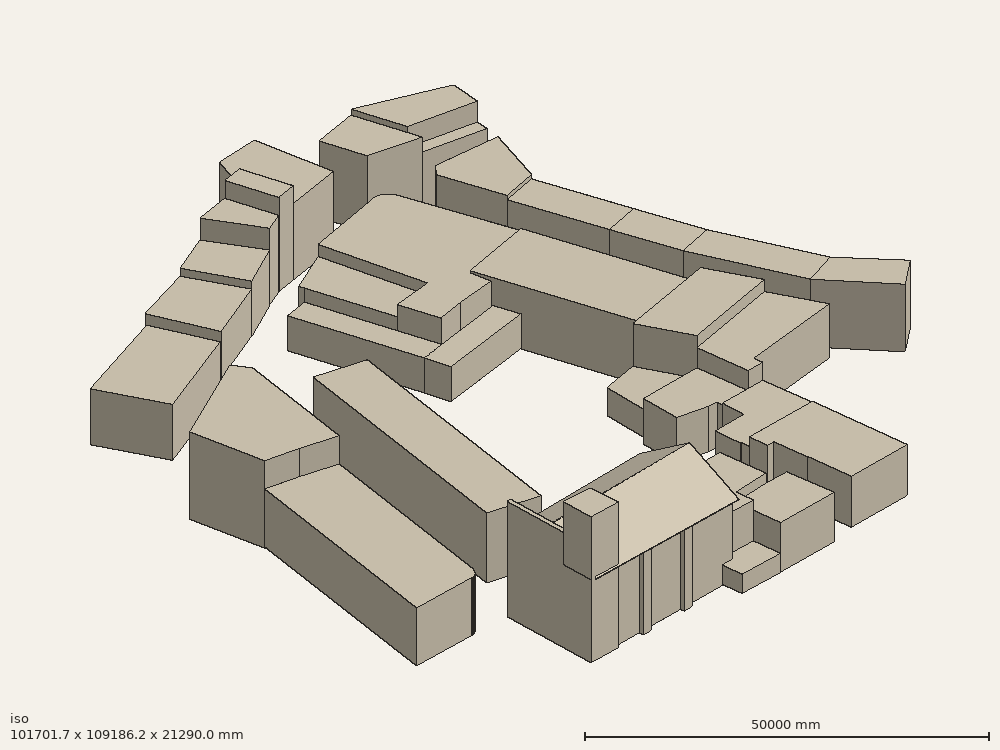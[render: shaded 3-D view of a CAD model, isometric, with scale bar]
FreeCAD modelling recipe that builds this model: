
FCSTD DOCUMENT  (FreeCAD 0.16R6563 (Git))
Label: Levantamento
License: All rights reserved
LicenseURL: http://en.wikipedia.org/wiki/All_rights_reserved
objects: App::Annotation×611, Part::Feature×158, Part::Part2DObjectPython×64, Part::Extrusion×37, App::DocumentObjectGroup×6, App::FeaturePython×4, Part::FeaturePython×3, Part::Cut×2, Part::Compound×1, Part::MultiFuse×1, App::DocumentObjectGroupPython×1
note: 269 computed .brp shape members not serialized (recipe doc carries the construction recipe); baked Part::Feature solids carry a one-line shape summary decoded from their .brp

FEATURE [App::Annotation] Text
  LabelText = TRAVESSA DE S.TIAGO
  Position = (-9.7511e+07,-6.33971e+07,25950)
FEATURE [App::Annotation] Text001
  LabelText = LARGO DR. JUSTINO FREIRE
  Position = (-9.75583e+07,-6.3388e+07,26154)
FEATURE [App::Annotation] Text002
  LabelText = RUA DO ALEIXO
  Position = (-9.75352e+07,-6.33613e+07,25958)
FEATURE [App::Annotation] Text003
  LabelText = RUA DO TERREIRINHO
  Position = (-9.75126e+07,-6.33096e+07,25667)
FEATURE [App::Annotation] Text004
  LabelText = RUA SERPA PINTO
  Position = (-9.74773e+07,-6.3325e+07,26806)
FEATURE [App::Annotation] Text005
  LabelText = IGREJA DE S. TIAGO
  Position = (-9.75165e+07,-6.33832e+07,25950)
FEATURE [App::Annotation] Text006
  LabelText = -97400
  Position = (-9.74009e+07,-6.34097e+07,0)
FEATURE [App::Annotation] Text007
  LabelText = -97450
  Position = (-9.74508e+07,-6.34097e+07,0)
FEATURE [App::Annotation] Text008
  LabelText = -97500
  Position = (-9.75009e+07,-6.34097e+07,0)
FEATURE [App::Annotation] Text009
  LabelText = -97550
  Position = (-9.75507e+07,-6.34097e+07,0)
FEATURE [App::Annotation] Text010
  LabelText = -63400
  Position = (-9.73992e+07,-6.33989e+07,0)
FEATURE [App::Annotation] Text011
  LabelText = -63350
  Position = (-9.73992e+07,-6.33486e+07,0)
FEATURE [App::Annotation] Text012
  LabelText = -63300
  Position = (-9.73992e+07,-6.32985e+07,0)
FEATURE [App::Annotation] Text013
  LabelText = VD
  Position = (-9.75235e+07,-6.33229e+07,0)
FEATURE [App::Annotation] Text014
  LabelText = 25.74
  Position = (-9.75242e+07,-6.33231e+07,0)
FEATURE [App::Annotation] Text015
  LabelText = IN
  Position = (-9.75237e+07,-6.33233e+07,0)
FEATURE [App::Annotation] Text016
  LabelText = 25.75
  Position = (-9.75244e+07,-6.33234e+07,0)
FEATURE [App::Annotation] Text017
  LabelText = LNMRVD
  Position = (-9.75268e+07,-6.3332e+07,0)
FEATURE [App::Annotation] Text018
  LabelText = 25.79
  Position = (-9.75274e+07,-6.33329e+07,0)
FEATURE [App::Annotation] Text019
  LabelText = LN
  Position = (-9.7528e+07,-6.33353e+07,0)
FEATURE [App::Annotation] Text020
  LabelText = 25.72
  Position = (-9.75287e+07,-6.33356e+07,0)
FEATURE [App::Annotation] Text021
  LabelText = 26.02
  Position = (-9.7542e+07,-6.33754e+07,0)
FEATURE [App::Annotation] Text022
  LabelText = CX
  Position = (-9.75309e+07,-6.33164e+07,0)
FEATURE [App::Annotation] Text023
  LabelText = 25.70
  Position = (-9.75313e+07,-6.33168e+07,0)
FEATURE [App::Annotation] Text024
  LabelText = CX
  Position = (-9.75307e+07,-6.33169e+07,0)
FEATURE [App::Annotation] Text025
  LabelText = 25.63
  Position = (-9.75311e+07,-6.33173e+07,0)
FEATURE [App::Annotation] Text026
  LabelText = CX
  Position = (-9.75311e+07,-6.3317e+07,0)
FEATURE [App::Annotation] Text027
  LabelText = 25.63
  Position = (-9.75315e+07,-6.33174e+07,0)
FEATURE [App::Annotation] Text028
  LabelText = CC
  Position = (-9.7534e+07,-6.33179e+07,0)
FEATURE [App::Annotation] Text029
  LabelText = 25.76
  Position = (-9.75346e+07,-6.33182e+07,0)
FEATURE [App::Annotation] Text030
  LabelText = OL
  Position = (-9.75349e+07,-6.33183e+07,0)
FEATURE [App::Annotation] Text031
  LabelText = 26.00
  Position = (-9.75356e+07,-6.33185e+07,0)
FEATURE [App::Annotation] Text032
  LabelText = OL
  Position = (-9.75364e+07,-6.3319e+07,0)
FEATURE [App::Annotation] Text033
  LabelText = 26.00
  Position = (-9.75371e+07,-6.33193e+07,0)
FEATURE [App::Annotation] Text034
  LabelText = LNCC
  Position = (-9.7539e+07,-6.33199e+07,0)
FEATURE [App::Annotation] Text035
  LabelText = 25.84
  Position = (-9.75396e+07,-6.33204e+07,0)
FEATURE [App::Annotation] Text036
  LabelText = LN
  Position = (-9.75385e+07,-6.33211e+07,0)
FEATURE [App::Annotation] Text037
  LabelText = 25.73
  Position = (-9.75392e+07,-6.33213e+07,0)
FEATURE [App::Annotation] Text038
  LabelText = CTT
  Position = (-9.75428e+07,-6.33239e+07,0)
FEATURE [App::Annotation] Text039
  LabelText = 25.88
  Position = (-9.75435e+07,-6.33242e+07,0)
FEATURE [App::Annotation] Text040
  LabelText = CTT
  Position = (-9.75436e+07,-6.33243e+07,0)
FEATURE [App::Annotation] Text041
  LabelText = 25.88
  Position = (-9.75442e+07,-6.33246e+07,0)
FEATURE [App::Annotation] Text042
  LabelText = CTT
  Position = (-9.75439e+07,-6.33237e+07,0)
FEATURE [App::Annotation] Text043
  LabelText = 25.87
  Position = (-9.75445e+07,-6.3324e+07,0)
FEATURE [App::Annotation] Text044
  LabelText = SOL
  Position = (-9.75449e+07,-6.33228e+07,0)
FEATURE [App::Annotation] Text045
  LabelText = 26.13
  Position = (-9.75455e+07,-6.33231e+07,0)
FEATURE [App::Annotation] Text046
  LabelText = LN
  Position = (-9.75498e+07,-6.33263e+07,0)
FEATURE [App::Annotation] Text047
  LabelText = 25.92
  Position = (-9.75505e+07,-6.33265e+07,0)
FEATURE [App::Annotation] Text048
  LabelText = CC
  Position = (-9.75503e+07,-6.33253e+07,0)
FEATURE [App::Annotation] Text049
  LabelText = 26.11
  Position = (-9.75509e+07,-6.33256e+07,0)
FEATURE [App::Annotation] Text050
  LabelText = OL
  Position = (-9.75518e+07,-6.3326e+07,0)
FEATURE [App::Annotation] Text051
  LabelText = 26.19
  Position = (-9.75524e+07,-6.33263e+07,0)
FEATURE [App::Annotation] Text052
  LabelText = CC
  Position = (-9.75559e+07,-6.33278e+07,0)
FEATURE [App::Annotation] Text053
  LabelText = 26.12
  Position = (-9.75565e+07,-6.3328e+07,0)
FEATURE [App::Annotation] Text054
  LabelText = LN
  Position = (-9.75554e+07,-6.33287e+07,0)
FEATURE [App::Annotation] Text055
  LabelText = 25.90
  Position = (-9.75561e+07,-6.33289e+07,0)
FEATURE [App::Annotation] Text056
  LabelText = INH
  Position = (-9.75539e+07,-6.3334e+07,0)
FEATURE [App::Annotation] Text057
  LabelText = 25.92
  Position = (-9.75546e+07,-6.33343e+07,0)
FEATURE [App::Annotation] Text058
  LabelText = INH
  Position = (-9.75549e+07,-6.33321e+07,0)
FEATURE [App::Annotation] Text059
  LabelText = 26.04
  Position = (-9.75555e+07,-6.33324e+07,0)
FEATURE [App::Annotation] Text060
  LabelText = INH
  Position = (-9.75501e+07,-6.33302e+07,0)
FEATURE [App::Annotation] Text061
  LabelText = 26.05
  Position = (-9.75508e+07,-6.33305e+07,0)
FEATURE [App::Annotation] Text062
  LabelText = INH
  Position = (-9.75369e+07,-6.33231e+07,0)
FEATURE [App::Annotation] Text063
  LabelText = 25.84
  Position = (-9.75376e+07,-6.33234e+07,0)
FEATURE [App::Annotation] Text064
  LabelText = INH
  Position = (-9.75357e+07,-6.33232e+07,0)
FEATURE [App::Annotation] Text065
  LabelText = 25.82
  Position = (-9.75363e+07,-6.33235e+07,0)
FEATURE [App::Annotation] Text066
  LabelText = INH
  Position = (-9.75336e+07,-6.33221e+07,0)
FEATURE [App::Annotation] Text067
  LabelText = 25.76
  Position = (-9.75343e+07,-6.33224e+07,0)
FEATURE [App::Annotation] Text068
  LabelText = OL
  Position = (-9.7533e+07,-6.33256e+07,0)
FEATURE [App::Annotation] Text069
  LabelText = 26.42
  Position = (-9.75337e+07,-6.33259e+07,0)
FEATURE [App::Annotation] Text070
  LabelText = IN
  Position = (-9.75314e+07,-6.33278e+07,0)
FEATURE [App::Annotation] Text071
  LabelText = 25.89
  Position = (-9.7532e+07,-6.33279e+07,0)
FEATURE [App::Annotation] Text072
  LabelText = CC
  Position = (-9.75315e+07,-6.33268e+07,0)
FEATURE [App::Annotation] Text073
  LabelText = 25.89
  Position = (-9.75322e+07,-6.33271e+07,0)
FEATURE [App::Annotation] Text074
  LabelText = CC
  Position = (-9.75329e+07,-6.33242e+07,0)
FEATURE [App::Annotation] Text075
  LabelText = 25.84
  Position = (-9.75336e+07,-6.33245e+07,0)
FEATURE [App::Annotation] Text076
  LabelText = CC
  Position = (-9.75382e+07,-6.33271e+07,0)
FEATURE [App::Annotation] Text077
  LabelText = 25.93
  Position = (-9.75388e+07,-6.33273e+07,0)
FEATURE [App::Annotation] Text078
  LabelText = UM
  Position = (-9.75385e+07,-6.33265e+07,0)
FEATURE [App::Annotation] Text079
  LabelText = 25.76
  Position = (-9.75392e+07,-6.33268e+07,0)
FEATURE [App::Annotation] Text080
  LabelText = UM
  Position = (-9.75319e+07,-6.33228e+07,0)
FEATURE [App::Annotation] Text081
  LabelText = 25.67
  Position = (-9.75326e+07,-6.33231e+07,0)
FEATURE [App::Annotation] Text082
  LabelText = UM
  Position = (-9.75313e+07,-6.33232e+07,0)
FEATURE [App::Annotation] Text083
  LabelText = 25.67
  Position = (-9.7532e+07,-6.33235e+07,0)
FEATURE [App::Annotation] Text084
  LabelText = LN
  Position = (-9.75323e+07,-6.33233e+07,0)
FEATURE [App::Annotation] Text085
  LabelText = 25.68
  Position = (-9.7533e+07,-6.33235e+07,0)
FEATURE [App::Annotation] Text086
  LabelText = LN
  Position = (-9.75315e+07,-6.33235e+07,0)
FEATURE [App::Annotation] Text087
  LabelText = 25.72
  Position = (-9.75322e+07,-6.33238e+07,0)
FEATURE [App::Annotation] Text088
  LabelText = LN
  Position = (-9.75305e+07,-6.33251e+07,0)
FEATURE [App::Annotation] Text089
  LabelText = 25.75
  Position = (-9.75311e+07,-6.33253e+07,0)
FEATURE [App::Annotation] Text090
  LabelText = LN
  Position = (-9.75301e+07,-6.33276e+07,0)
FEATURE [App::Annotation] Text091
  LabelText = 25.72
  Position = (-9.75307e+07,-6.33279e+07,0)
FEATURE [App::Annotation] Text092
  LabelText = VD
  Position = (-9.75244e+07,-6.33212e+07,0)
FEATURE [App::Annotation] Text093
  LabelText = 25.72
  Position = (-9.75251e+07,-6.33214e+07,0)
FEATURE [App::Annotation] Text094
  LabelText = CXD
  Position = (-9.75204e+07,-6.33159e+07,0)
FEATURE [App::Annotation] Text095
  LabelText = 25.67
  Position = (-9.75207e+07,-6.33163e+07,0)
FEATURE [App::Annotation] Text096
  LabelText = VD
  Position = (-9.75183e+07,-6.33166e+07,0)
FEATURE [App::Annotation] Text097
  LabelText = 25.58
  Position = (-9.7519e+07,-6.33169e+07,0)
FEATURE [App::Annotation] Text098
  LabelText = OL
  Position = (-9.75059e+07,-6.33029e+07,0)
FEATURE [App::Annotation] Text099
  LabelText = 25.84
  Position = (-9.75065e+07,-6.33031e+07,0)
FEATURE [App::Annotation] Text100
  LabelText = OL
  Position = (-9.75043e+07,-6.33022e+07,0)
FEATURE [App::Annotation] Text101
  LabelText = 25.94
  Position = (-9.75049e+07,-6.33025e+07,0)
FEATURE [App::Annotation] Text102
  LabelText = CXE
  Position = (-9.7504e+07,-6.33017e+07,0)
FEATURE [App::Annotation] Text103
  LabelText = 25.84
  Position = (-9.75043e+07,-6.33021e+07,0)
FEATURE [App::Annotation] Text104
  LabelText = CXE
  Position = (-9.75038e+07,-6.3302e+07,0)
FEATURE [App::Annotation] Text105
  LabelText = 25.79
  Position = (-9.75041e+07,-6.33024e+07,0)
FEATURE [App::Annotation] Text106
  LabelText = CXE
  Position = (-9.7503e+07,-6.33016e+07,0)
FEATURE [App::Annotation] Text107
  LabelText = 25.80
  Position = (-9.75033e+07,-6.3302e+07,0)
FEATURE [App::Annotation] Text108
  LabelText = OL
  Position = (-9.7499e+07,-6.32997e+07,0)
FEATURE [App::Annotation] Text109
  LabelText = 26.17
  Position = (-9.74996e+07,-6.32999e+07,0)
FEATURE [App::Annotation] Text110
  LabelText = CXD
  Position = (-9.75007e+07,-6.33004e+07,0)
FEATURE [App::Annotation] Text111
  LabelText = 25.85
  Position = (-9.7501e+07,-6.3301e+07,0)
FEATURE [App::Annotation] Text112
  LabelText = CXD
  Position = (-9.74978e+07,-6.32998e+07,0)
FEATURE [App::Annotation] Text113
  LabelText = 25.86
  Position = (-9.74982e+07,-6.33003e+07,0)
FEATURE [App::Annotation] Text114
  LabelText = UM
  Position = (-9.74967e+07,-6.33e+07,0)
FEATURE [App::Annotation] Text115
  LabelText = 25.80
  Position = (-9.74974e+07,-6.33003e+07,0)
FEATURE [App::Annotation] Text116
  LabelText = UM
  Position = (-9.74961e+07,-6.32999e+07,0)
FEATURE [App::Annotation] Text117
  LabelText = 25.79
  Position = (-9.74968e+07,-6.33001e+07,0)
FEATURE [App::Annotation] Text118
  LabelText = IN
  Position = (-9.74906e+07,-6.32984e+07,0)
FEATURE [App::Annotation] Text119
  LabelText = 26.00
  Position = (-9.74913e+07,-6.32985e+07,0)
FEATURE [App::Annotation] Text120
  LabelText = CC
  Position = (-9.74881e+07,-6.32975e+07,0)
FEATURE [App::Annotation] Text121
  LabelText = 26.01
  Position = (-9.74887e+07,-6.32978e+07,0)
FEATURE [App::Annotation] Text122
  LabelText = VD
  Position = (-9.74883e+07,-6.33016e+07,0)
FEATURE [App::Annotation] Text123
  LabelText = 26.02
  Position = (-9.7489e+07,-6.33019e+07,0)
FEATURE [App::Annotation] Text124
  LabelText = VD
  Position = (-9.74956e+07,-6.33036e+07,0)
FEATURE [App::Annotation] Text125
  LabelText = 25.93
  Position = (-9.74963e+07,-6.33039e+07,0)
FEATURE [App::Annotation] Text126
  LabelText = VD
  Position = (-9.74956e+07,-6.33036e+07,0)
FEATURE [App::Annotation] Text127
  LabelText = 25.93
  Position = (-9.74963e+07,-6.33039e+07,0)
FEATURE [App::Annotation] Text128
  LabelText = CXD
  Position = (-9.75007e+07,-6.33052e+07,0)
FEATURE [App::Annotation] Text129
  LabelText = 25.82
  Position = (-9.7501e+07,-6.33056e+07,0)
FEATURE [App::Annotation] Text130
  LabelText = VD
  Position = (-9.75015e+07,-6.33054e+07,0)
FEATURE [App::Annotation] Text131
  LabelText = 25.83
  Position = (-9.75022e+07,-6.33057e+07,0)
FEATURE [App::Annotation] Text132
  LabelText = VD
  Position = (-9.75047e+07,-6.33071e+07,0)
FEATURE [App::Annotation] Text133
  LabelText = 25.76
  Position = (-9.75053e+07,-6.33073e+07,0)
FEATURE [App::Annotation] Text134
  LabelText = CC
  Position = (-9.74996e+07,-6.33064e+07,0)
FEATURE [App::Annotation] Text135
  LabelText = 25.89
  Position = (-9.75003e+07,-6.33067e+07,0)
FEATURE [App::Annotation] Text136
  LabelText = VD
  Position = (-9.75005e+07,-6.33068e+07,0)
FEATURE [App::Annotation] Text137
  LabelText = 25.84
  Position = (-9.75012e+07,-6.3307e+07,0)
FEATURE [App::Annotation] Text138
  LabelText = MRVD
  Position = (-9.75264e+07,-6.33325e+07,0)
FEATURE [App::Annotation] Text139
  LabelText = 26.39
  Position = (-9.7527e+07,-6.33331e+07,0)
FEATURE [App::Annotation] Text140
  LabelText = CT
  Position = (-9.75249e+07,-6.33283e+07,0)
FEATURE [App::Annotation] Text141
  LabelText = 26.35
  Position = (-9.75255e+07,-6.33286e+07,0)
FEATURE [App::Annotation] Text142
  LabelText = CT
  Position = (-9.75222e+07,-6.33238e+07,0)
FEATURE [App::Annotation] Text143
  LabelText = 26.29
  Position = (-9.75229e+07,-6.3324e+07,0)
FEATURE [App::Annotation] Text144
  LabelText = CT
  Position = (-9.75189e+07,-6.33204e+07,0)
FEATURE [App::Annotation] Text145
  LabelText = 26.22
  Position = (-9.75196e+07,-6.33206e+07,0)
FEATURE [App::Annotation] Text146
  LabelText = CT
  Position = (-9.75162e+07,-6.33183e+07,0)
FEATURE [App::Annotation] Text147
  LabelText = 26.20
  Position = (-9.75169e+07,-6.33186e+07,0)
FEATURE [App::Annotation] Text148
  LabelText = CT
  Position = (-9.75164e+07,-6.33162e+07,0)
FEATURE [App::Annotation] Text149
  LabelText = 26.04
  Position = (-9.75171e+07,-6.33165e+07,0)
FEATURE [App::Annotation] Text150
  LabelText = CT
  Position = (-9.75151e+07,-6.33153e+07,0)
FEATURE [App::Annotation] Text151
  LabelText = 26.08
  Position = (-9.75157e+07,-6.33155e+07,0)
FEATURE [App::Annotation] Text152
  LabelText = IL
  Position = (-9.75163e+07,-6.33171e+07,0)
FEATURE [App::Annotation] Text153
  LabelText = 26.13
  Position = (-9.75169e+07,-6.33173e+07,0)
FEATURE [App::Annotation] Text154
  LabelText = IL
  Position = (-9.75157e+07,-6.3316e+07,0)
FEATURE [App::Annotation] Text155
  LabelText = 26.09
  Position = (-9.75164e+07,-6.33161e+07,0)
FEATURE [App::Annotation] Text156
  LabelText = CC
  Position = (-9.75107e+07,-6.33057e+07,0)
FEATURE [App::Annotation] Text157
  LabelText = 25.68
  Position = (-9.75113e+07,-6.3306e+07,0)
FEATURE [App::Annotation] Text158
  LabelText = AT
  Position = (-9.75124e+07,-6.33068e+07,0)
FEATURE [App::Annotation] Text159
  LabelText = 25.58
  Position = (-9.75131e+07,-6.33071e+07,0)
FEATURE [App::Annotation] Text160
  LabelText = OL
  Position = (-9.75161e+07,-6.33083e+07,0)
FEATURE [App::Annotation] Text161
  LabelText = 25.81
  Position = (-9.75167e+07,-6.33085e+07,0)
FEATURE [App::Annotation] Text162
  LabelText = AT
  Position = (-9.75195e+07,-6.33102e+07,0)
FEATURE [App::Annotation] Text163
  LabelText = 25.48
  Position = (-9.75202e+07,-6.33104e+07,0)
FEATURE [App::Annotation] Text164
  LabelText = CXCTT
  Position = (-9.75202e+07,-6.331e+07,0)
FEATURE [App::Annotation] Text165
  LabelText = 25.48
  Position = (-9.75202e+07,-6.33104e+07,0)
FEATURE [App::Annotation] Text166
  LabelText = CXCTT
  Position = (-9.75206e+07,-6.33102e+07,0)
FEATURE [App::Annotation] Text167
  LabelText = 25.47
  Position = (-9.75206e+07,-6.33106e+07,0)
FEATURE [App::Annotation] Text168
  LabelText = UM
  Position = (-9.75203e+07,-6.33103e+07,0)
FEATURE [App::Annotation] Text169
  LabelText = 25.38
  Position = (-9.7521e+07,-6.33106e+07,0)
FEATURE [App::Annotation] Text170
  LabelText = CC
  Position = (-9.75208e+07,-6.33104e+07,0)
FEATURE [App::Annotation] Text171
  LabelText = 25.47
  Position = (-9.75214e+07,-6.33106e+07,0)
FEATURE [App::Annotation] Text172
  LabelText = CTT
  Position = (-9.7521e+07,-6.33111e+07,0)
FEATURE [App::Annotation] Text173
  LabelText = 25.54
  Position = (-9.75216e+07,-6.33115e+07,0)
FEATURE [App::Annotation] Text174
  LabelText = CTT
  Position = (-9.75215e+07,-6.33114e+07,0)
FEATURE [App::Annotation] Text175
  LabelText = 25.57
  Position = (-9.75222e+07,-6.33118e+07,0)
FEATURE [App::Annotation] Text176
  LabelText = CTT
  Position = (-9.7522e+07,-6.33107e+07,0)
FEATURE [App::Annotation] Text177
  LabelText = 25.55
  Position = (-9.75226e+07,-6.3311e+07,0)
FEATURE [App::Annotation] Text178
  LabelText = CC
  Position = (-9.75249e+07,-6.33104e+07,0)
FEATURE [App::Annotation] Text179
  LabelText = 25.65
  Position = (-9.75256e+07,-6.33106e+07,0)
FEATURE [App::Annotation] Text180
  LabelText = OL
  Position = (-9.75244e+07,-6.33121e+07,0)
FEATURE [App::Annotation] Text181
  LabelText = 26.10
  Position = (-9.7525e+07,-6.33123e+07,0)
FEATURE [App::Annotation] Text182
  LabelText = G
  Position = (-9.7524e+07,-6.33116e+07,0)
FEATURE [App::Annotation] Text183
  LabelText = 25.61
  Position = (-9.75246e+07,-6.33117e+07,0)
FEATURE [App::Annotation] Text184
  LabelText = G
  Position = (-9.75238e+07,-6.33122e+07,0)
FEATURE [App::Annotation] Text185
  LabelText = G
  Position = (-9.7524e+07,-6.33123e+07,0)
FEATURE [App::Annotation] Text186
  LabelText = CC
  Position = (-9.75238e+07,-6.33134e+07,0)
FEATURE [App::Annotation] Text187
  LabelText = 25.54
  Position = (-9.75245e+07,-6.33136e+07,0)
FEATURE [App::Annotation] Text188
  LabelText = UM
  Position = (-9.75246e+07,-6.33138e+07,0)
FEATURE [App::Annotation] Text189
  LabelText = 25.52
  Position = (-9.75253e+07,-6.33141e+07,0)
FEATURE [App::Annotation] Text190
  LabelText = SOL
  Position = (-9.75262e+07,-6.33143e+07,0)
FEATURE [App::Annotation] Text191
  LabelText = 25.98
  Position = (-9.75268e+07,-6.33146e+07,0)
FEATURE [App::Annotation] Text192
  LabelText = CXE
  Position = (-9.75276e+07,-6.33148e+07,0)
FEATURE [App::Annotation] Text193
  LabelText = 25.69
  Position = (-9.75279e+07,-6.33152e+07,0)
FEATURE [App::Annotation] Text194
  LabelText = CXE
  Position = (-9.75275e+07,-6.33151e+07,0)
FEATURE [App::Annotation] Text195
  LabelText = 25.63
  Position = (-9.75278e+07,-6.33155e+07,0)
FEATURE [App::Annotation] Text196
  LabelText = CXE
  Position = (-9.75282e+07,-6.33154e+07,0)
FEATURE [App::Annotation] Text197
  LabelText = 25.63
  Position = (-9.75286e+07,-6.33158e+07,0)
FEATURE [App::Annotation] Text198
  LabelText = VD
  Position = (-9.75189e+07,-6.33146e+07,0)
FEATURE [App::Annotation] Text199
  LabelText = 25.64
  Position = (-9.75196e+07,-6.33149e+07,0)
FEATURE [App::Annotation] Text200
  LabelText = VD
  Position = (-9.75178e+07,-6.33139e+07,0)
FEATURE [App::Annotation] Text201
  LabelText = 25.69
  Position = (-9.75185e+07,-6.33141e+07,0)
FEATURE [App::Annotation] Text202
  LabelText = VD
  Position = (-9.75147e+07,-6.33122e+07,0)
FEATURE [App::Annotation] Text203
  LabelText = 25.65
  Position = (-9.75154e+07,-6.33124e+07,0)
FEATURE [App::Annotation] Text204
  LabelText = 25.59
  Position = (-9.75159e+07,-6.3314e+07,0)
FEATURE [App::Annotation] Text205
  LabelText = VD
  Position = (-9.75151e+07,-6.33139e+07,0)
FEATURE [App::Annotation] Text206
  LabelText = 25.60
  Position = (-9.75158e+07,-6.33142e+07,0)
FEATURE [App::Annotation] Text207
  LabelText = G
  Position = (-9.75151e+07,-6.33144e+07,0)
FEATURE [App::Annotation] Text208
  LabelText = 25.62
  Position = (-9.75158e+07,-6.33145e+07,0)
FEATURE [App::Annotation] Text209
  LabelText = G
  Position = (-9.7515e+07,-6.33146e+07,0)
FEATURE [App::Annotation] Text210
  LabelText = 25.81
  Position = (-9.75156e+07,-6.33147e+07,0)
FEATURE [App::Annotation] Text211
  LabelText = G
  Position = (-9.75148e+07,-6.3315e+07,0)
FEATURE [App::Annotation] Text212
  LabelText = 26.13
  Position = (-9.75154e+07,-6.33151e+07,0)
FEATURE [App::Annotation] Text213
  LabelText = G
  Position = (-9.75121e+07,-6.33136e+07,0)
FEATURE [App::Annotation] Text214
  LabelText = 26.12
  Position = (-9.75128e+07,-6.33137e+07,0)
FEATURE [App::Annotation] Text215
  LabelText = G
  Position = (-9.75123e+07,-6.33134e+07,0)
FEATURE [App::Annotation] Text216
  LabelText = 25.82
  Position = (-9.7513e+07,-6.33135e+07,0)
FEATURE [App::Annotation] Text217
  LabelText = G
  Position = (-9.75124e+07,-6.33131e+07,0)
FEATURE [App::Annotation] Text218
  LabelText = 25.65
  Position = (-9.75131e+07,-6.33132e+07,0)
FEATURE [App::Annotation] Text219
  LabelText = AMP
  Position = (-9.75137e+07,-6.33114e+07,0)
FEATURE [App::Annotation] Text220
  LabelText = 25.69
  Position = (-9.75144e+07,-6.33119e+07,0)
FEATURE [App::Annotation] Text221
  LabelText = AMP
  Position = (-9.75064e+07,-6.33077e+07,0)
FEATURE [App::Annotation] Text222
  LabelText = 25.77
  Position = (-9.75071e+07,-6.33081e+07,0)
FEATURE [App::Annotation] Text223
  LabelText = VD
  Position = (-9.7506e+07,-6.33096e+07,0)
FEATURE [App::Annotation] Text224
  LabelText = 25.99
  Position = (-9.75067e+07,-6.33099e+07,0)
FEATURE [App::Annotation] Text225
  LabelText = MR
  Position = (-9.7506e+07,-6.33102e+07,0)
FEATURE [App::Annotation] Text226
  LabelText = 26.07
  Position = (-9.75067e+07,-6.33104e+07,0)
FEATURE [App::Annotation] Text227
  LabelText = MRCC
  Position = (-9.75003e+07,-6.33069e+07,0)
FEATURE [App::Annotation] Text228
  LabelText = 26.23
  Position = (-9.7501e+07,-6.33075e+07,0)
FEATURE [App::Annotation] Text229
  LabelText = ESTMR
  Position = (-9.75051e+07,-6.33093e+07,0)
FEATURE [App::Annotation] Text230
  LabelText = 26.13
  Position = (-9.75051e+07,-6.33097e+07,0)
FEATURE [App::Annotation] Text231
  LabelText = EST
  Position = (-9.7502e+07,-6.33232e+07,0)
FEATURE [App::Annotation] Text232
  LabelText = 26.32
  Position = (-9.75023e+07,-6.33236e+07,0)
FEATURE [App::Annotation] Text233
  LabelText = CC
  Position = (-9.74969e+07,-6.33227e+07,0)
FEATURE [App::Annotation] Text234
  LabelText = 26.61
  Position = (-9.74975e+07,-6.3323e+07,0)
FEATURE [App::Annotation] Text235
  LabelText = IN20
  Position = (-9.74775e+07,-6.33355e+07,0)
FEATURE [App::Annotation] Text236
  LabelText = 26.83
  Position = (-9.74781e+07,-6.3336e+07,0)
FEATURE [App::Annotation] Text237
  LabelText = IN20
  Position = (-9.74755e+07,-6.33426e+07,0)
FEATURE [App::Annotation] Text238
  LabelText = 26.90
  Position = (-9.74762e+07,-6.3343e+07,0)
FEATURE [App::Annotation] Text239
  LabelText = IN20
  Position = (-9.74749e+07,-6.3345e+07,0)
FEATURE [App::Annotation] Text240
  LabelText = 26.90
  Position = (-9.74755e+07,-6.33455e+07,0)
FEATURE [App::Annotation] Text241
  LabelText = OL
  Position = (-9.7472e+07,-6.33367e+07,0)
FEATURE [App::Annotation] Text242
  LabelText = 26.86
  Position = (-9.74727e+07,-6.33369e+07,0)
FEATURE [App::Annotation] Text243
  LabelText = ESG
  Position = (-9.7474e+07,-6.33311e+07,0)
FEATURE [App::Annotation] Text244
  LabelText = 26.39
  Position = (-9.74743e+07,-6.33315e+07,0)
FEATURE [App::Annotation] Text245
  LabelText = OL
  Position = (-9.74741e+07,-6.3329e+07,0)
FEATURE [App::Annotation] Text246
  LabelText = 26.56
  Position = (-9.74748e+07,-6.33293e+07,0)
FEATURE [App::Annotation] Text247
  LabelText = OL
  Position = (-9.74748e+07,-6.33265e+07,0)
FEATURE [App::Annotation] Text248
  LabelText = 26.58
  Position = (-9.74754e+07,-6.33267e+07,0)
FEATURE [App::Annotation] Text249
  LabelText = OL
  Position = (-9.74762e+07,-6.33213e+07,0)
FEATURE [App::Annotation] Text250
  LabelText = 26.54
  Position = (-9.74768e+07,-6.33215e+07,0)
FEATURE [App::Annotation] Text251
  LabelText = CC
  Position = (-9.74793e+07,-6.33223e+07,0)
FEATURE [App::Annotation] Text252
  LabelText = 26.39
  Position = (-9.748e+07,-6.33225e+07,0)
FEATURE [App::Annotation] Text253
  LabelText = AT
  Position = (-9.74791e+07,-6.33222e+07,0)
FEATURE [App::Annotation] Text254
  LabelText = 26.35
  Position = (-9.74798e+07,-6.33225e+07,0)
FEATURE [App::Annotation] Text255
  LabelText = AT
  Position = (-9.74772e+07,-6.33305e+07,0)
FEATURE [App::Annotation] Text256
  LabelText = 26.52
  Position = (-9.74779e+07,-6.33307e+07,0)
FEATURE [App::Annotation] Text257
  LabelText = UM25
  Position = (-9.74767e+07,-6.33302e+07,0)
FEATURE [App::Annotation] Text258
  LabelText = 26.44
  Position = (-9.74774e+07,-6.33308e+07,0)
FEATURE [App::Annotation] Text259
  LabelText = UM25
  Position = (-9.74765e+07,-6.33309e+07,0)
FEATURE [App::Annotation] Text260
  LabelText = 26.47
  Position = (-9.74772e+07,-6.33315e+07,0)
FEATURE [App::Annotation] Text261
  LabelText = UM25
  Position = (-9.74765e+07,-6.33309e+07,0)
FEATURE [App::Annotation] Text262
  LabelText = 26.47
  Position = (-9.74772e+07,-6.33315e+07,0)
FEATURE [App::Annotation] Text263
  LabelText = CC
  Position = (-9.74772e+07,-6.33312e+07,0)
FEATURE [App::Annotation] Text264
  LabelText = 26.51
  Position = (-9.74778e+07,-6.33314e+07,0)
FEATURE [App::Annotation] Text265
  LabelText = AT
  Position = (-9.74769e+07,-6.33311e+07,0)
FEATURE [App::Annotation] Text266
  LabelText = 26.50
  Position = (-9.74776e+07,-6.33314e+07,0)
FEATURE [App::Annotation] Text267
  LabelText = AT
  Position = (-9.74755e+07,-6.33378e+07,0)
FEATURE [App::Annotation] Text268
  LabelText = 26.62
  Position = (-9.74761e+07,-6.33381e+07,0)
FEATURE [App::Annotation] Text269
  LabelText = AT
  Position = (-9.74751e+07,-6.33389e+07,0)
FEATURE [App::Annotation] Text270
  LabelText = 26.69
  Position = (-9.74758e+07,-6.33391e+07,0)
FEATURE [App::Annotation] Text271
  LabelText = CX
  Position = (-9.74751e+07,-6.33372e+07,0)
FEATURE [App::Annotation] Text272
  LabelText = 26.61
  Position = (-9.74754e+07,-6.33376e+07,0)
FEATURE [App::Annotation] Text273
  LabelText = OL
  Position = (-9.74711e+07,-6.33401e+07,0)
FEATURE [App::Annotation] Text274
  LabelText = 26.84
  Position = (-9.74718e+07,-6.33404e+07,0)
FEATURE [App::Annotation] Text275
  LabelText = UM25
  Position = (-9.74713e+07,-6.33411e+07,0)
FEATURE [App::Annotation] Text276
  LabelText = 26.71
  Position = (-9.74719e+07,-6.33416e+07,0)
FEATURE [App::Annotation] Text277
  LabelText = UM25
  Position = (-9.74711e+07,-6.33417e+07,0)
FEATURE [App::Annotation] Text278
  LabelText = 26.73
  Position = (-9.74718e+07,-6.33423e+07,0)
FEATURE [App::Annotation] Text279
  LabelText = CC
  Position = (-9.74707e+07,-6.3342e+07,0)
FEATURE [App::Annotation] Text280
  LabelText = 26.76
  Position = (-9.74714e+07,-6.33422e+07,0)
FEATURE [App::Annotation] Text281
  LabelText = OL
  Position = (-9.74678e+07,-6.33494e+07,0)
FEATURE [App::Annotation] Text282
  LabelText = 27.04
  Position = (-9.74685e+07,-6.33497e+07,0)
FEATURE [App::Annotation] Text283
  LabelText = CX
  Position = (-9.74687e+07,-6.33501e+07,0)
FEATURE [App::Annotation] Text284
  LabelText = 27.04
  Position = (-9.74691e+07,-6.33505e+07,0)
FEATURE [App::Annotation] Text285
  LabelText = CC
  Position = (-9.74661e+07,-6.33623e+07,0)
FEATURE [App::Annotation] Text286
  LabelText = 27.55
  Position = (-9.74668e+07,-6.33626e+07,0)
FEATURE [App::Annotation] Text287
  LabelText = OL
  Position = (-9.74678e+07,-6.33585e+07,0)
FEATURE [App::Annotation] Text288
  LabelText = 27.40
  Position = (-9.74685e+07,-6.33587e+07,0)
FEATURE [App::Annotation] Text289
  LabelText = OL
  Position = (-9.74727e+07,-6.33483e+07,0)
FEATURE [App::Annotation] Text290
  LabelText = 27.14
  Position = (-9.74734e+07,-6.33485e+07,0)
FEATURE [App::Annotation] Text291
  LabelText = CX
  Position = (-9.74726e+07,-6.33461e+07,0)
FEATURE [App::Annotation] Text292
  LabelText = 26.85
  Position = (-9.7473e+07,-6.33465e+07,0)
FEATURE [App::Annotation] Text293
  LabelText = UM25
  Position = (-9.74731e+07,-6.3345e+07,0)
FEATURE [App::Annotation] Text294
  LabelText = 26.81
  Position = (-9.74736e+07,-6.33456e+07,0)
FEATURE [App::Annotation] Text295
  LabelText = UM25
  Position = (-9.74729e+07,-6.33456e+07,0)
FEATURE [App::Annotation] Text296
  LabelText = 26.80
  Position = (-9.74736e+07,-6.33462e+07,0)
FEATURE [App::Annotation] Text297
  LabelText = AT
  Position = (-9.74731e+07,-6.33466e+07,0)
FEATURE [App::Annotation] Text298
  LabelText = 26.87
  Position = (-9.74737e+07,-6.33469e+07,0)
FEATURE [App::Annotation] Text299
  LabelText = CC
  Position = (-9.74731e+07,-6.3347e+07,0)
FEATURE [App::Annotation] Text300
  LabelText = 26.89
  Position = (-9.74738e+07,-6.33472e+07,0)
FEATURE [App::Annotation] Text301
  LabelText = CC
  Position = (-9.74733e+07,-6.33461e+07,0)
FEATURE [App::Annotation] Text302
  LabelText = 26.87
  Position = (-9.7474e+07,-6.33463e+07,0)
FEATURE [App::Annotation] Text303
  LabelText = CC30
  Position = (-9.74747e+07,-6.33462e+07,0)
FEATURE [App::Annotation] Text304
  LabelText = 26.91
  Position = (-9.74752e+07,-6.33467e+07,0)
FEATURE [App::Annotation] Text305
  LabelText = EST
  Position = (-9.75057e+07,-6.33385e+07,0)
FEATURE [App::Annotation] Text306
  LabelText = CC
  Position = (-9.75033e+07,-6.33238e+07,0)
FEATURE [App::Annotation] Text307
  LabelText = 26.29
  Position = (-9.75039e+07,-6.33241e+07,0)
FEATURE [App::Annotation] Text308
  LabelText = ESTA
  Position = (-9.75136e+07,-6.33216e+07,0)
FEATURE [App::Annotation] Text309
  LabelText = 26.22
  Position = (-9.75138e+07,-6.3322e+07,0)
FEATURE [App::Annotation] Text310
  LabelText = ESTA
  Position = (-9.75146e+07,-6.33204e+07,0)
FEATURE [App::Annotation] Text311
  LabelText = 26.22
  Position = (-9.75147e+07,-6.33208e+07,0)
FEATURE [App::Annotation] Text312
  LabelText = ESTA
  Position = (-9.75106e+07,-6.33181e+07,0)
FEATURE [App::Annotation] Text313
  LabelText = 26.19
  Position = (-9.75107e+07,-6.33185e+07,0)
FEATURE [App::Annotation] Text314
  LabelText = ESTA
  Position = (-9.75125e+07,-6.33137e+07,0)
FEATURE [App::Annotation] Text315
  LabelText = 26.09
  Position = (-9.75127e+07,-6.33141e+07,0)
FEATURE [App::Annotation] Text316
  LabelText = ESTA
  Position = (-9.75168e+07,-6.33177e+07,0)
FEATURE [App::Annotation] Text317
  LabelText = 26.15
  Position = (-9.75169e+07,-6.33181e+07,0)
FEATURE [App::Annotation] Text318
  LabelText = ESTA
  Position = (-9.75135e+07,-6.33216e+07,0)
FEATURE [App::Annotation] Text319
  LabelText = 26.22
  Position = (-9.75137e+07,-6.3322e+07,0)
FEATURE [App::Annotation] Text320
  LabelText = ESTA
  Position = (-9.75199e+07,-6.33285e+07,0)
FEATURE [App::Annotation] Text321
  LabelText = 26.34
  Position = (-9.75201e+07,-6.33289e+07,0)
FEATURE [App::Annotation] Text322
  LabelText = ESTA
  Position = (-9.75246e+07,-6.33266e+07,0)
FEATURE [App::Annotation] Text323
  LabelText = 26.29
  Position = (-9.75248e+07,-6.3327e+07,0)
FEATURE [App::Annotation] Text324
  LabelText = ESTA
  Position = (-9.75272e+07,-6.33333e+07,0)
FEATURE [App::Annotation] Text325
  LabelText = 26.37
  Position = (-9.75274e+07,-6.33337e+07,0)
FEATURE [App::Annotation] Text326
  LabelText = ESTA
  Position = (-9.75217e+07,-6.33327e+07,0)
FEATURE [App::Annotation] Text327
  LabelText = 26.38
  Position = (-9.75219e+07,-6.33331e+07,0)
FEATURE [App::Annotation] Text328
  LabelText = ESTA
  Position = (-9.75307e+07,-6.33502e+07,0)
FEATURE [App::Annotation] Text329
  LabelText = 26.37
  Position = (-9.75309e+07,-6.33506e+07,0)
FEATURE [App::Annotation] Text330
  LabelText = ESTA
  Position = (-9.75255e+07,-6.33497e+07,0)
FEATURE [App::Annotation] Text331
  LabelText = 26.34
  Position = (-9.75257e+07,-6.33501e+07,0)
FEATURE [App::Annotation] Text332
  LabelText = ESTA1
  Position = (-9.75292e+07,-6.33666e+07,0)
FEATURE [App::Annotation] Text333
  LabelText = 26.09
  Position = (-9.75293e+07,-6.3367e+07,0)
FEATURE [App::Annotation] Text334
  LabelText = ESTA1
  Position = (-9.75342e+07,-6.33669e+07,0)
FEATURE [App::Annotation] Text335
  LabelText = 26.08
  Position = (-9.75343e+07,-6.33673e+07,0)
FEATURE [App::Annotation] Text336
  LabelText = ESTA1
  Position = (-9.75059e+07,-6.33539e+07,0)
FEATURE [App::Annotation] Text337
  LabelText = 26.29
  Position = (-9.7506e+07,-6.33543e+07,0)
FEATURE [App::Annotation] Text338
  LabelText = ESTA1
  Position = (-9.75009e+07,-6.33537e+07,0)
FEATURE [App::Annotation] Text339
  LabelText = 26.37
  Position = (-9.7501e+07,-6.33541e+07,0)
FEATURE [App::Annotation] Text340
  LabelText = ESTA1
  Position = (-9.75013e+07,-6.33551e+07,0)
FEATURE [App::Annotation] Text341
  LabelText = 26.35
  Position = (-9.75014e+07,-6.33555e+07,0)
FEATURE [App::Annotation] Text342
  LabelText = ESTA1
  Position = (-9.7499e+07,-6.33554e+07,0)
FEATURE [App::Annotation] Text343
  LabelText = 26.41
  Position = (-9.74991e+07,-6.33558e+07,0)
FEATURE [App::Annotation] Text344
  LabelText = ESTA1
  Position = (-9.75019e+07,-6.33694e+07,0)
FEATURE [App::Annotation] Text345
  LabelText = 26.33
  Position = (-9.7502e+07,-6.33698e+07,0)
FEATURE [App::Annotation] Text346
  LabelText = ESTA1
  Position = (-9.75042e+07,-6.33689e+07,0)
FEATURE [App::Annotation] Text347
  LabelText = 26.31
  Position = (-9.75042e+07,-6.33693e+07,0)
FEATURE [App::Annotation] Text348
  LabelText = ESTA1
  Position = (-9.75046e+07,-6.33704e+07,0)
FEATURE [App::Annotation] Text349
  LabelText = 26.31
  Position = (-9.75046e+07,-6.33708e+07,0)
FEATURE [App::Annotation] Text350
  LabelText = ESTA1
  Position = (-9.75096e+07,-6.33706e+07,0)
FEATURE [App::Annotation] Text351
  LabelText = 26.24
  Position = (-9.75097e+07,-6.33715e+07,0)
FEATURE [App::Annotation] Text352
  LabelText = ESTA
  Position = (-9.7515e+07,-6.33713e+07,0)
FEATURE [App::Annotation] Text353
  LabelText = 26.19
  Position = (-9.75151e+07,-6.33722e+07,0)
FEATURE [App::Annotation] Text354
  LabelText = ESTA
  Position = (-9.75098e+07,-6.33473e+07,0)
FEATURE [App::Annotation] Text355
  LabelText = 26.37
  Position = (-9.751e+07,-6.33477e+07,0)
FEATURE [App::Annotation] Text356
  LabelText = ESTA
  Position = (-9.7514e+07,-6.33445e+07,0)
FEATURE [App::Annotation] Text357
  LabelText = 26.40
  Position = (-9.75142e+07,-6.33449e+07,0)
FEATURE [App::Annotation] Text358
  LabelText = ESTA
  Position = (-9.75182e+07,-6.33417e+07,0)
FEATURE [App::Annotation] Text359
  LabelText = 26.39
  Position = (-9.75184e+07,-6.33421e+07,0)
FEATURE [App::Annotation] Text360
  LabelText = ESTA
  Position = (-9.75156e+07,-6.33297e+07,0)
FEATURE [App::Annotation] Text361
  LabelText = 26.37
  Position = (-9.75158e+07,-6.33301e+07,0)
FEATURE [App::Annotation] Text362
  LabelText = ESTA
  Position = (-9.75134e+07,-6.33311e+07,0)
FEATURE [App::Annotation] Text363
  LabelText = 26.37
  Position = (-9.75136e+07,-6.33315e+07,0)
FEATURE [App::Annotation] Text364
  LabelText = ESTA
  Position = (-9.75125e+07,-6.33262e+07,0)
FEATURE [App::Annotation] Text365
  LabelText = 26.30
  Position = (-9.75127e+07,-6.33266e+07,0)
FEATURE [App::Annotation] Text366
  LabelText = ESTA
  Position = (-9.75061e+07,-6.33303e+07,0)
FEATURE [App::Annotation] Text367
  LabelText = 26.34
  Position = (-9.75063e+07,-6.33307e+07,0)
FEATURE [App::Annotation] Text368
  LabelText = EST
  Position = (-9.75055e+07,-6.3311e+07,0)
FEATURE [App::Annotation] Text369
  LabelText = 26.14
  Position = (-9.75065e+07,-6.33115e+07,0)
FEATURE [App::Annotation] Text370
  LabelText = ESTA
  Position = (-9.75e+07,-6.3334e+07,0)
FEATURE [App::Annotation] Text371
  LabelText = 26.46
  Position = (-9.75001e+07,-6.33344e+07,0)
FEATURE [App::Annotation] Text372
  LabelText = ESTA
  Position = (-9.75031e+07,-6.33302e+07,0)
FEATURE [App::Annotation] Text373
  LabelText = 26.35
  Position = (-9.75033e+07,-6.33306e+07,0)
FEATURE [App::Annotation] Text374
  LabelText = ESTA
  Position = (-9.74924e+07,-6.3328e+07,0)
FEATURE [App::Annotation] Text375
  LabelText = 26.65
  Position = (-9.74926e+07,-6.33284e+07,0)
FEATURE [App::Annotation] Text376
  LabelText = ESTA1
  Position = (-9.74896e+07,-6.33315e+07,0)
FEATURE [App::Annotation] Text377
  LabelText = 26.73
  Position = (-9.74897e+07,-6.33319e+07,0)
FEATURE [App::Annotation] Text378
  LabelText = ESTA
  Position = (-9.75049e+07,-6.33496e+07,0)
FEATURE [App::Annotation] Text379
  LabelText = 26.33
  Position = (-9.7505e+07,-6.335e+07,0)
FEATURE [App::Annotation] Text380
  LabelText = ESTA
  Position = (-9.75028e+07,-6.33394e+07,0)
FEATURE [App::Annotation] Text381
  LabelText = 26.38
  Position = (-9.7503e+07,-6.33398e+07,0)
FEATURE [App::Annotation] Text382
  LabelText = ESTA
  Position = (-9.74874e+07,-6.33358e+07,0)
FEATURE [App::Annotation] Text383
  LabelText = 26.82
  Position = (-9.74876e+07,-6.33362e+07,0)
FEATURE [App::Annotation] Text384
  LabelText = ESTA
  Position = (-9.74859e+07,-6.33402e+07,0)
FEATURE [App::Annotation] Text385
  LabelText = 26.85
  Position = (-9.74861e+07,-6.33406e+07,0)
FEATURE [App::Annotation] Text386
  LabelText = ESTA1
  Position = (-9.7487e+07,-6.33453e+07,0)
FEATURE [App::Annotation] Text387
  LabelText = 26.88
  Position = (-9.74871e+07,-6.33457e+07,0)
FEATURE [App::Annotation] Text388
  LabelText = ESTA
  Position = (-9.74752e+07,-6.33434e+07,0)
FEATURE [App::Annotation] Text389
  LabelText = 26.88
  Position = (-9.74753e+07,-6.33439e+07,0)
FEATURE [App::Annotation] Text390
  LabelText = ESTA
  Position = (-9.74803e+07,-6.33453e+07,0)
FEATURE [App::Annotation] Text391
  LabelText = 26.96
  Position = (-9.74805e+07,-6.33457e+07,0)
FEATURE [App::Annotation] Text392
  LabelText = ESTA
  Position = (-9.74849e+07,-6.33267e+07,0)
FEATURE [App::Annotation] Text393
  LabelText = 26.76
  Position = (-9.74851e+07,-6.33271e+07,0)
FEATURE [App::Annotation] Text394
  LabelText = ESTA
  Position = (-9.74808e+07,-6.33249e+07,0)
FEATURE [App::Annotation] Text395
  LabelText = 26.77
  Position = (-9.74809e+07,-6.33253e+07,0)
FEATURE [App::Annotation] Text396
  LabelText = LA
  Position = (-9.74935e+07,-6.33286e+07,0)
FEATURE [App::Annotation] Text397
  LabelText = 26.62
  Position = (-9.74942e+07,-6.33288e+07,0)
FEATURE [App::Annotation] Text398
  LabelText = LA
  Position = (-9.75015e+07,-6.33305e+07,0)
FEATURE [App::Annotation] Text399
  LabelText = CC
  Position = (-9.75017e+07,-6.33301e+07,0)
FEATURE [App::Annotation] Text400
  LabelText = 26.38
  Position = (-9.75024e+07,-6.33303e+07,0)
FEATURE [App::Annotation] Text401
  LabelText = CC
  Position = (-9.74973e+07,-6.3329e+07,0)
FEATURE [App::Annotation] Text402
  LabelText = 26.53
  Position = (-9.7498e+07,-6.33293e+07,0)
FEATURE [App::Annotation] Text403
  LabelText = CC
  Position = (-9.7491e+07,-6.3328e+07,0)
FEATURE [App::Annotation] Text404
  LabelText = 26.72
  Position = (-9.74917e+07,-6.33283e+07,0)
FEATURE [App::Annotation] Text405
  LabelText = VDCC
  Position = (-9.74806e+07,-6.33224e+07,0)
FEATURE [App::Annotation] Text406
  LabelText = 26.98
  Position = (-9.74813e+07,-6.3323e+07,0)
FEATURE [App::Annotation] Text407
  LabelText = VD
  Position = (-9.74788e+07,-6.33311e+07,0)
FEATURE [App::Annotation] Text408
  LabelText = 26.76
  Position = (-9.74794e+07,-6.33314e+07,0)
FEATURE [App::Annotation] Text409
  LabelText = VD
  Position = (-9.74778e+07,-6.33331e+07,0)
FEATURE [App::Annotation] Text410
  LabelText = 26.79
  Position = (-9.74785e+07,-6.33333e+07,0)
FEATURE [App::Annotation] Text411
  LabelText = VD
  Position = (-9.74762e+07,-6.33344e+07,0)
FEATURE [App::Annotation] Text412
  LabelText = 26.63
  Position = (-9.74769e+07,-6.33346e+07,0)
FEATURE [App::Annotation] Text413
  LabelText = CONTADOR
  Position = (-9.74801e+07,-6.33344e+07,0)
FEATURE [App::Annotation] Text414
  LabelText = 26.87
  Position = (-9.74807e+07,-6.33351e+07,0)
FEATURE [App::Annotation] Text415
  LabelText = EST
  Position = (-9.74739e+07,-6.33358e+07,0)
FEATURE [App::Annotation] Text416
  LabelText = 26.61
  Position = (-9.74742e+07,-6.33352e+07,0)
FEATURE [App::Annotation] Text417
  LabelText = CC1
  Position = (-9.74875e+07,-6.33497e+07,0)
FEATURE [App::Annotation] Text418
  LabelText = 26.84
  Position = (-9.74881e+07,-6.33501e+07,0)
FEATURE [App::Annotation] Text419
  LabelText = CC1
  Position = (-9.74951e+07,-6.33518e+07,0)
FEATURE [App::Annotation] Text420
  LabelText = 26.69
  Position = (-9.74955e+07,-6.3352e+07,0)
FEATURE [App::Annotation] Text421
  LabelText = CC1
  Position = (-9.74949e+07,-6.33803e+07,0)
FEATURE [App::Annotation] Text422
  LabelText = 26.53
  Position = (-9.74956e+07,-6.33807e+07,0)
FEATURE [App::Annotation] Text423
  LabelText = CC1
  Position = (-9.74931e+07,-6.33927e+07,0)
FEATURE [App::Annotation] Text424
  LabelText = 26.60
  Position = (-9.74936e+07,-6.3393e+07,0)
FEATURE [App::Annotation] Text425
  LabelText = CC
  Position = (-9.74967e+07,-6.33856e+07,0)
FEATURE [App::Annotation] Text426
  LabelText = 26.56
  Position = (-9.74974e+07,-6.33859e+07,0)
FEATURE [App::Annotation] Text427
  LabelText = EST
  Position = (-9.74989e+07,-6.33722e+07,0)
FEATURE [App::Annotation] Text428
  LabelText = 26.41
  Position = (-9.74991e+07,-6.33715e+07,0)
FEATURE [App::Annotation] Text429
  LabelText = EST
  Position = (-9.7506e+07,-6.33433e+07,0)
FEATURE [App::Annotation] Text430
  LabelText = 26.38
  Position = (-9.75062e+07,-6.33426e+07,0)
FEATURE [App::Annotation] Text431
  LabelText = 26.37
  Position = (-9.75059e+07,-6.33377e+07,0)
FEATURE [App::Annotation] Text432
  LabelText = CC17
  Position = (-9.74952e+07,-6.33756e+07,0)
FEATURE [App::Annotation] Text433
  LabelText = 26.48
  Position = (-9.74958e+07,-6.33761e+07,0)
FEATURE [App::Annotation] Text434
  LabelText = CC
  Position = (-9.75012e+07,-6.33733e+07,0)
FEATURE [App::Annotation] Text435
  LabelText = 26.34
  Position = (-9.75018e+07,-6.33736e+07,0)
FEATURE [App::Annotation] Text436
  LabelText = OL
  Position = (-9.75341e+07,-6.33344e+07,0)
FEATURE [App::Annotation] Text437
  LabelText = 26.31
  Position = (-9.75347e+07,-6.33347e+07,0)
FEATURE [App::Annotation] Text438
  LabelText = OL
  Position = (-9.75352e+07,-6.33395e+07,0)
FEATURE [App::Annotation] Text439
  LabelText = 26.40
  Position = (-9.75359e+07,-6.33397e+07,0)
FEATURE [App::Annotation] Text440
  LabelText = OL
  Position = (-9.75368e+07,-6.335e+07,0)
FEATURE [App::Annotation] Text441
  LabelText = 26.32
  Position = (-9.75375e+07,-6.33503e+07,0)
FEATURE [App::Annotation] Text442
  LabelText = OL
  Position = (-9.75384e+07,-6.33561e+07,0)
FEATURE [App::Annotation] Text443
  LabelText = 26.33
  Position = (-9.75391e+07,-6.33563e+07,0)
FEATURE [App::Annotation] Text444
  LabelText = OL
  Position = (-9.75397e+07,-6.33628e+07,0)
FEATURE [App::Annotation] Text445
  LabelText = 26.32
  Position = (-9.75404e+07,-6.3363e+07,0)
FEATURE [App::Annotation] Text446
  LabelText = OL
  Position = (-9.75413e+07,-6.33692e+07,0)
FEATURE [App::Annotation] Text447
  LabelText = 26.32
  Position = (-9.7542e+07,-6.33695e+07,0)
FEATURE [App::Annotation] Text448
  LabelText = OL
  Position = (-9.75436e+07,-6.3377e+07,0)
FEATURE [App::Annotation] Text449
  LabelText = 26.31
  Position = (-9.75442e+07,-6.33773e+07,0)
FEATURE [App::Annotation] Text450
  LabelText = EST
  Position = (-9.75417e+07,-6.3375e+07,0)
FEATURE [App::Annotation] Text451
  LabelText = LN
  Position = (-9.75355e+07,-6.33694e+07,0)
FEATURE [App::Annotation] Text452
  LabelText = 25.80
  Position = (-9.75362e+07,-6.33697e+07,0)
FEATURE [App::Annotation] Text453
  LabelText = EL
  Position = (-9.75339e+07,-6.33679e+07,0)
FEATURE [App::Annotation] Text454
  LabelText = 26.12
  Position = (-9.75346e+07,-6.33681e+07,0)
FEATURE [App::Annotation] Text455
  LabelText = IN
  Position = (-9.75341e+07,-6.33686e+07,0)
FEATURE [App::Annotation] Text456
  LabelText = 26.10
  Position = (-9.75347e+07,-6.33687e+07,0)
FEATURE [App::Annotation] Text457
  LabelText = MR30
  Position = (-9.75347e+07,-6.33683e+07,0)
FEATURE [App::Annotation] Text458
  LabelText = 25.89
  Position = (-9.75354e+07,-6.33689e+07,0)
FEATURE [App::Annotation] Text459
  LabelText = CC
  Position = (-9.75423e+07,-6.33759e+07,0)
FEATURE [App::Annotation] Text460
  LabelText = 26.01
  Position = (-9.75429e+07,-6.33761e+07,0)
FEATURE [App::Annotation] Text461
  LabelText = CC
  Position = (-9.75428e+07,-6.33768e+07,0)
FEATURE [App::Annotation] Text462
  LabelText = 25.98
  Position = (-9.75434e+07,-6.3377e+07,0)
FEATURE [App::Annotation] Text463
  LabelText = LN
  Position = (-9.75434e+07,-6.33787e+07,0)
FEATURE [App::Annotation] Text464
  LabelText = 25.75
  Position = (-9.75441e+07,-6.33789e+07,0)
FEATURE [App::Annotation] Text465
  LabelText = LN
  Position = (-9.75421e+07,-6.33784e+07,0)
FEATURE [App::Annotation] Text466
  LabelText = 25.75
  Position = (-9.75427e+07,-6.33786e+07,0)
FEATURE [App::Annotation] Text467
  LabelText = LN
  Position = (-9.75411e+07,-6.33776e+07,0)
FEATURE [App::Annotation] Text468
  LabelText = 25.75
  Position = (-9.75418e+07,-6.33778e+07,0)
FEATURE [App::Annotation] Text469
  LabelText = EST
  Position = (-9.75287e+07,-6.33165e+07,0)
FEATURE [App::Annotation] Text470
  LabelText = 25.63
  Position = (-9.75289e+07,-6.33172e+07,0)
FEATURE [App::Annotation] Text471
  LabelText = CXA
  Position = (-9.75259e+07,-6.33149e+07,0)
FEATURE [App::Annotation] Text472
  LabelText = 25.58
  Position = (-9.75262e+07,-6.33153e+07,0)
FEATURE [App::Annotation] Text473
  LabelText = CXA
  Position = (-9.75249e+07,-6.33171e+07,0)
FEATURE [App::Annotation] Text474
  LabelText = 25.67
  Position = (-9.75252e+07,-6.33175e+07,0)
FEATURE [App::Annotation] Text475
  LabelText = CXD
  Position = (-9.75267e+07,-6.33196e+07,0)
FEATURE [App::Annotation] Text476
  LabelText = 25.69
  Position = (-9.7527e+07,-6.33201e+07,0)
FEATURE [App::Annotation] Text477
  LabelText = VD
  Position = (-9.75251e+07,-6.33223e+07,0)
FEATURE [App::Annotation] Text478
  LabelText = 25.68
  Position = (-9.75258e+07,-6.33226e+07,0)
FEATURE [App::Annotation] Text479
  LabelText = CXD
  Position = (-9.75291e+07,-6.33237e+07,0)
FEATURE [App::Annotation] Text480
  LabelText = 25.71
  Position = (-9.75294e+07,-6.33241e+07,0)
FEATURE [App::Annotation] Text481
  LabelText = UM25
  Position = (-9.75314e+07,-6.33351e+07,0)
FEATURE [App::Annotation] Text482
  LabelText = 25.63
  Position = (-9.75321e+07,-6.33357e+07,0)
FEATURE [App::Annotation] Text483
  LabelText = UM25
  Position = (-9.75313e+07,-6.33344e+07,0)
FEATURE [App::Annotation] Text484
  LabelText = 25.62
  Position = (-9.75319e+07,-6.3335e+07,0)
FEATURE [App::Annotation] Text485
  LabelText = UM25
  Position = (-9.75284e+07,-6.33347e+07,0)
FEATURE [App::Annotation] Text486
  LabelText = 25.63
  Position = (-9.7529e+07,-6.33352e+07,0)
FEATURE [App::Annotation] Text487
  LabelText = UM25
  Position = (-9.75286e+07,-6.33353e+07,0)
FEATURE [App::Annotation] Text488
  LabelText = 25.63
  Position = (-9.75292e+07,-6.33358e+07,0)
FEATURE [App::Annotation] Text489
  LabelText = CXD
  Position = (-9.7531e+07,-6.33399e+07,0)
FEATURE [App::Annotation] Text490
  LabelText = 25.73
  Position = (-9.75313e+07,-6.33403e+07,0)
FEATURE [App::Annotation] Text491
  LabelText = CXA
  Position = (-9.75337e+07,-6.33483e+07,0)
FEATURE [App::Annotation] Text492
  LabelText = 25.74
  Position = (-9.7534e+07,-6.33488e+07,0)
FEATURE [App::Annotation] Text493
  LabelText = UM25
  Position = (-9.75346e+07,-6.33492e+07,0)
FEATURE [App::Annotation] Text494
  LabelText = 25.64
  Position = (-9.75352e+07,-6.33498e+07,0)
FEATURE [App::Annotation] Text495
  LabelText = UM25
  Position = (-9.75347e+07,-6.33498e+07,0)
FEATURE [App::Annotation] Text496
  LabelText = 25.65
  Position = (-9.75354e+07,-6.33504e+07,0)
FEATURE [App::Annotation] Text497
  LabelText = UM25
  Position = (-9.75319e+07,-6.33506e+07,0)
FEATURE [App::Annotation] Text498
  LabelText = 25.66
  Position = (-9.75325e+07,-6.33512e+07,0)
FEATURE [App::Annotation] Text499
  LabelText = UM25
  Position = (-9.75317e+07,-6.335e+07,0)
FEATURE [App::Annotation] Text500
  LabelText = 25.67
  Position = (-9.75324e+07,-6.33505e+07,0)
FEATURE [App::Annotation] Text501
  LabelText = VD
  Position = (-9.75314e+07,-6.33498e+07,0)
FEATURE [App::Annotation] Text502
  LabelText = 25.64
  Position = (-9.75321e+07,-6.335e+07,0)
FEATURE [App::Annotation] Text503
  LabelText = VD
  Position = (-9.75349e+07,-6.33655e+07,0)
FEATURE [App::Annotation] Text504
  LabelText = 25.75
  Position = (-9.75364e+07,-6.33657e+07,0)
FEATURE [App::Annotation] Text505
  LabelText = UM25
  Position = (-9.75352e+07,-6.33658e+07,0)
FEATURE [App::Annotation] Text506
  LabelText = 25.74
  Position = (-9.75358e+07,-6.33663e+07,0)
FEATURE [App::Annotation] Text507
  LabelText = UM25
  Position = (-9.75353e+07,-6.33664e+07,0)
FEATURE [App::Annotation] Text508
  LabelText = 25.74
  Position = (-9.7536e+07,-6.3367e+07,0)
FEATURE [App::Annotation] Text509
  LabelText = UM25
  Position = (-9.75381e+07,-6.33651e+07,0)
FEATURE [App::Annotation] Text510
  LabelText = 25.70
  Position = (-9.75387e+07,-6.33657e+07,0)
FEATURE [App::Annotation] Text511
  LabelText = UM25
  Position = (-9.75382e+07,-6.33658e+07,0)
FEATURE [App::Annotation] Text512
  LabelText = 25.70
  Position = (-9.75388e+07,-6.33663e+07,0)
FEATURE [App::Annotation] Text513
  LabelText = CXA
  Position = (-9.75394e+07,-6.3373e+07,0)
FEATURE [App::Annotation] Text514
  LabelText = 25.79
  Position = (-9.75397e+07,-6.33734e+07,0)
FEATURE [App::Annotation] Text515
  LabelText = UM25
  Position = (-9.75412e+07,-6.33778e+07,0)
FEATURE [App::Annotation] Text516
  LabelText = 25.71
  Position = (-9.75417e+07,-6.33784e+07,0)
FEATURE [App::Annotation] Text517
  LabelText = UM25
  Position = (-9.75417e+07,-6.33783e+07,0)
FEATURE [App::Annotation] Text518
  LabelText = 25.72
  Position = (-9.75423e+07,-6.33789e+07,0)
FEATURE [App::Annotation] Text519
  LabelText = CX
  Position = (-9.75411e+07,-6.33968e+07,0)
FEATURE [App::Annotation] Text520
  LabelText = 25.97
  Position = (-9.75415e+07,-6.33972e+07,0)
FEATURE [App::Annotation] Text521
  LabelText = CC
  Position = (-9.75383e+07,-6.33929e+07,0)
FEATURE [App::Annotation] Text522
  LabelText = 25.86
  Position = (-9.7539e+07,-6.33932e+07,0)
FEATURE [App::Annotation] Text523
  LabelText = CX
  Position = (-9.75414e+07,-6.3386e+07,0)
FEATURE [App::Annotation] Text524
  LabelText = 25.84
  Position = (-9.75419e+07,-6.33864e+07,0)
FEATURE [App::Annotation] Text525
  LabelText = OL
  Position = (-9.75374e+07,-6.33856e+07,0)
FEATURE [App::Annotation] Text526
  LabelText = 25.94
  Position = (-9.75381e+07,-6.33858e+07,0)
FEATURE [App::Annotation] Text527
  LabelText = CC
  Position = (-9.75459e+07,-6.33963e+07,0)
FEATURE [App::Annotation] Text528
  LabelText = 25.95
  Position = (-9.75466e+07,-6.33966e+07,0)
FEATURE [App::Annotation] Text529
  LabelText = LN
  Position = (-9.75463e+07,-6.33948e+07,0)
FEATURE [App::Annotation] Text530
  LabelText = 25.83
  Position = (-9.7547e+07,-6.3395e+07,0)
FEATURE [App::Annotation] Text531
  LabelText = LNS
  Position = (-9.75404e+07,-6.33928e+07,0)
FEATURE [App::Annotation] Text532
  LabelText = 25.87
  Position = (-9.75411e+07,-6.33932e+07,0)
FEATURE [App::Annotation] Text533
  LabelText = UM25
  Position = (-9.75392e+07,-6.33803e+07,0)
FEATURE [App::Annotation] Text534
  LabelText = 25.67
  Position = (-9.75398e+07,-6.33808e+07,0)
FEATURE [App::Annotation] Text535
  LabelText = UM25
  Position = (-9.75391e+07,-6.33796e+07,0)
FEATURE [App::Annotation] Text536
  LabelText = 25.67
  Position = (-9.75398e+07,-6.33801e+07,0)
FEATURE [App::Annotation] Text537
  LabelText = LN
  Position = (-9.75386e+07,-6.33793e+07,0)
FEATURE [App::Annotation] Text538
  LabelText = 25.76
  Position = (-9.75393e+07,-6.33795e+07,0)
FEATURE [App::Annotation] Text539
  LabelText = LN
  Position = (-9.75382e+07,-6.33783e+07,0)
FEATURE [App::Annotation] Text540
  LabelText = 25.81
  Position = (-9.75388e+07,-6.33786e+07,0)
FEATURE [App::Annotation] Text541
  LabelText = CCLN
  Position = (-9.75376e+07,-6.33772e+07,0)
FEATURE [App::Annotation] Text542
  LabelText = 25.83
  Position = (-9.75383e+07,-6.33777e+07,0)
FEATURE [App::Annotation] Text543
  LabelText = IN
  Position = (-9.75376e+07,-6.33773e+07,0)
FEATURE [App::Annotation] Text544
  LabelText = LN
  Position = (-9.75371e+07,-6.33769e+07,0)
FEATURE [App::Annotation] Text545
  LabelText = 25.82
  Position = (-9.75378e+07,-6.33772e+07,0)
FEATURE [App::Annotation] Text546
  LabelText = MR47
  Position = (-9.75365e+07,-6.33765e+07,0)
FEATURE [App::Annotation] Text547
  LabelText = 25.84
  Position = (-9.75367e+07,-6.33771e+07,0)
FEATURE [App::Annotation] Text548
  LabelText = CC
  Position = (-9.75353e+07,-6.33773e+07,0)
FEATURE [App::Annotation] Text549
  LabelText = CC
  Position = (-9.75295e+07,-6.33777e+07,0)
FEATURE [App::Annotation] Text550
  LabelText = 26.05
  Position = (-9.753e+07,-6.3378e+07,0)
FEATURE [App::Annotation] Text551
  LabelText = CC
  Position = (-9.75295e+07,-6.33769e+07,0)
FEATURE [App::Annotation] Text552
  LabelText = 26.04
  Position = (-9.75301e+07,-6.33772e+07,0)
FEATURE [App::Annotation] Text553
  LabelText = CC
  Position = (-9.75279e+07,-6.33768e+07,0)
FEATURE [App::Annotation] Text554
  LabelText = 26.04
  Position = (-9.75286e+07,-6.3377e+07,0)
FEATURE [App::Annotation] Text555
  LabelText = CC
  Position = (-9.75223e+07,-6.33771e+07,0)
FEATURE [App::Annotation] Text556
  LabelText = 26.05
  Position = (-9.75228e+07,-6.33773e+07,0)
FEATURE [App::Annotation] Text557
  LabelText = VDCC
  Position = (-9.75224e+07,-6.33759e+07,0)
FEATURE [App::Annotation] Text558
  LabelText = 26.10
  Position = (-9.7523e+07,-6.33764e+07,0)
FEATURE [App::Annotation] Text559
  LabelText = VD
  Position = (-9.75123e+07,-6.33737e+07,0)
FEATURE [App::Annotation] Text560
  LabelText = 26.22
  Position = (-9.75129e+07,-6.3374e+07,0)
FEATURE [App::Annotation] Text561
  LabelText = CC
  Position = (-9.75132e+07,-6.3374e+07,0)
FEATURE [App::Annotation] Text562
  LabelText = 26.20
  Position = (-9.75139e+07,-6.33742e+07,0)
FEATURE [App::Annotation] Text563
  LabelText = RUA FRANCISCO XAVIER DE MELO
  Position = (-9.75529e+07,-6.33302e+07,25667)
FEATURE [App::Annotation] Text564
  LabelText = RUA DOS CELEIROS STA.MARIA
  Position = (-9.7528e+07,-6.32978e+07,25667)
FEATURE [App::Annotation] Text565
  LabelText = RUA ROQUE FERREIRA LOBO
  Position = (-9.74884e+07,-6.32816e+07,25667)
FEATURE [App::Annotation] Text566
  LabelText = PRA?A MACHADO SANTOS
  Position = (-9.75324e+07,-6.34081e+07,25950)
FEATURE [App::Annotation] Text567
  LabelText = RUA JOS? EDUARDO C?SAR
  Position = (-9.74795e+07,-6.34012e+07,25950)
FEATURE [App::Annotation] Text568
  LabelText = sol.
  Position = (-9.74712e+07,-6.33398e+07,0)
FEATURE [App::Annotation] Text569
  LabelText = sol.
  Position = (-9.74721e+07,-6.33364e+07,0)
FEATURE [App::Annotation] Text570
  LabelText = sol.
  Position = (-9.74741e+07,-6.33287e+07,0)
FEATURE [App::Annotation] Text571
  LabelText = sol.
  Position = (-9.74748e+07,-6.33262e+07,0)
FEATURE [App::Annotation] Text572
  LabelText = sol.
  Position = (-9.74761e+07,-6.3321e+07,0)
FEATURE [App::Annotation] Text573
  LabelText = sol.
  Position = (-9.74732e+07,-6.3349e+07,0)
FEATURE [App::Annotation] Text574
  LabelText = sol.
  Position = (-9.74679e+07,-6.33491e+07,0)
FEATURE [App::Annotation] Text575
  LabelText = sol.
  Position = (-9.74685e+07,-6.33593e+07,0)
FEATURE [App::Annotation] Text576
  LabelText = sol.
  Position = (-9.74992e+07,-6.32994e+07,0)
FEATURE [App::Annotation] Text577
  LabelText = sol.
  Position = (-9.75063e+07,-6.33027e+07,0)
FEATURE [App::Annotation] Text578
  LabelText = sol.
  Position = (-9.75051e+07,-6.33019e+07,0)
FEATURE [App::Annotation] Text579
  LabelText = sol.
  Position = (-9.75164e+07,-6.33079e+07,0)
FEATURE [App::Annotation] Text580
  LabelText = sol.
  Position = (-9.75354e+07,-6.33181e+07,0)
FEATURE [App::Annotation] Text581
  LabelText = sol.
  Position = (-9.75368e+07,-6.33188e+07,0)
FEATURE [App::Annotation] Text582
  LabelText = sol.
  Position = (-9.75251e+07,-6.33127e+07,0)
FEATURE [App::Annotation] Text583
  LabelText = sol.
  Position = (-9.75333e+07,-6.33264e+07,0)
FEATURE [App::Annotation] Text584
  LabelText = sol.
  Position = (-9.75344e+07,-6.33342e+07,0)
FEATURE [App::Annotation] Text585
  LabelText = sol.
  Position = (-9.75355e+07,-6.33393e+07,0)
FEATURE [App::Annotation] Text586
  LabelText = sol.
  Position = (-9.75373e+07,-6.33498e+07,0)
FEATURE [App::Annotation] Text587
  LabelText = sol.
  Position = (-9.75387e+07,-6.33558e+07,0)
FEATURE [App::Annotation] Text588
  LabelText = sol.
  Position = (-9.75401e+07,-6.33625e+07,0)
FEATURE [App::Annotation] Text589
  LabelText = sol.
  Position = (-9.75416e+07,-6.3369e+07,0)
FEATURE [App::Annotation] Text590
  LabelText = sol.
  Position = (-9.75441e+07,-6.33768e+07,0)
FEATURE [App::Annotation] Text591
  LabelText = 1
  Position = (-9.75384e+07,-6.33771e+07,0)
FEATURE [App::Annotation] Text592
  LabelText = 2
  Position = (-9.75247e+07,-6.33245e+07,0)
FEATURE [App::Annotation] Text593
  LabelText = 3
  Position = (-9.75167e+07,-6.33149e+07,0)
FEATURE [App::Annotation] Text594
  LabelText = 4
  Position = (-9.75e+07,-6.33065e+07,0)
FEATURE [App::Annotation] Text595
  LabelText = 5
  Position = (-9.74979e+07,-6.33225e+07,0)
FEATURE [App::Annotation] Text596
  LabelText = 6
  Position = (-9.7504e+07,-6.33251e+07,0)
FEATURE [App::Annotation] Text597
  LabelText = 7
  Position = (-9.75028e+07,-6.33301e+07,0)
FEATURE [App::Annotation] Text598
  LabelText = 8
  Position = (-9.74908e+07,-6.33276e+07,0)
FEATURE [App::Annotation] Text599
  LabelText = 9
  Position = (-9.74909e+07,-6.33259e+07,0)
FEATURE [App::Annotation] Text600
  LabelText = 10
  Position = (-9.74789e+07,-6.33236e+07,0)
FEATURE [App::Annotation] Text601
  LabelText = 11
  Position = (-9.74735e+07,-6.3345e+07,0)
FEATURE [App::Annotation] Text602
  LabelText = 12
  Position = (-9.74964e+07,-6.33532e+07,0)
FEATURE [App::Annotation] Text603
  LabelText = 13
  Position = (-9.75009e+07,-6.33748e+07,0)
FEATURE [App::Annotation] Text604
  LabelText = sol.
  Position = (-9.75376e+07,-6.33853e+07,0)
FEATURE [App::Annotation] Text605
  LabelText = 14
  Position = (-9.75142e+07,-6.33736e+07,0)
FEATURE [App::Annotation] Text606
  LabelText = Antiga Casa Hip?lito
  Position = (314401,56114.9,0)
FEATURE [App::Annotation] Text607
  LabelText = Torres Vedras
  Position = (321944,49195.3,0)
FEATURE [App::Annotation] Text608
  LabelText = Escala 1:500
  Position = (323553,19226.1,0)
FEATURE [App::Annotation] Text609
  LabelText = 2002
  Position = (333363,12993.3,0)
FEATURE [App::Annotation] Text610
  LabelText = Planta de Localiza??o
  Position = (312374,26727,0)
FEATURE [Part::Feature] ENTITIES_CAIXAS_DE_VISITA
  shape: bbox 76470 x 104400 x 2e-07 mm, 0 faces, 0 solids (baked)
FEATURE [Part::Feature] ENTITIES_CAIXAS_DIVERSAS_ELECT_E_TELEC__
  shape: bbox 60800 x 26520 x 2e-07 mm, 0 faces, 0 solids (baked)
FEATURE [Part::Feature] ENTITIES_DEGRAUS
  shape: bbox 12350 x 3383 x 2e-07 mm, 0 faces, 0 solids (baked)
FEATURE [Part::Feature] ENTITIES_ESTACIONAMENTOS
  shape: bbox 59010 x 63050 x 2e-07 mm, 0 faces, 0 solids (baked)
FEATURE [Part::Feature] ENTITIES_ESTACOES
  shape: bbox 68020 x 64590 x 2e-07 mm, 0 faces, 0 solids (baked)
FEATURE [Part::Feature] ENTITIES_HATCH
  shape: bbox 100400 x 110500 x 2e-07 mm, 0 faces, 0 solids (baked)
FEATURE [Part::Feature] ENTITIES_LANCIS
  shape: bbox 90170 x 116100 x 2e-07 mm, 0 faces, 0 solids (baked)
FEATURE [Part::Feature] ENTITIES_MALHA_DE_COORDENADAS
  shape: bbox 155000 x 105000 x 2e-07 mm, 0 faces, 0 solids (baked)
FEATURE [Part::Feature] ENTITIES_MUROS
  shape: bbox 6523 x 3774 x 2e-07 mm, 0 faces, 0 solids (baked)
FEATURE [Part::Feature] ENTITIES_PINOS
  shape: bbox 41630 x 29570 x 2e-07 mm, 0 faces, 0 solids (baked)
FEATURE [Part::Feature] ENTITIES_RAMPA
  shape: bbox 7683 x 5072 x 2e-07 mm, 0 faces, 0 solids (baked)
FEATURE [Part::Feature] ENTITIES_SUMIDOUROS
  shape: bbox 70950 x 80960 x 2e-07 mm, 0 faces, 0 solids (baked)
FEATURE [Part::Feature] ENTITIES_TALUDES
  shape: bbox 10170 x 13920 x 2e-07 mm, 0 faces, 0 solids (baked)
FEATURE [Part::Feature] ENTITIES_TOPONIMIA
  shape: bbox 9405 x 7785 x 2e-07 mm, 0 faces, 0 solids (baked)
FEATURE [Part::Feature] ENTITIES_VEDA__ES
  shape: bbox 46580 x 74580 x 2e-07 mm, 0 faces, 0 solids (baked)
FEATURE [Part::Feature] ENTITIES_ZIGUEZAGUES
  shape: bbox 21980 x 11910 x 2e-07 mm, 0 faces, 0 solids (baked)
FEATURE [Part::Feature] ENTITIES___REA_INTERVEN__O
  shape: bbox 63760 x 86960 x 2e-07 mm, 0 faces, 0 solids (baked)
FEATURE [Part::Feature] ENTITIES_pontos
  shape: bbox 89790 x 99440 x 2e-07 mm, 0 faces, 0 solids (baked)
FEATURE [App::DocumentObjectGroup] Group  label="Textos"
  Group = -> [Text610,Text002,Text011,Text012,Text003,Text010,Text071,Text100,Text101,Text160,Text161,Text162,Text163,Text166,Text164,Text165,Text167,Text131,Text132,Text133,Text134,Text098,Text099,Text066,Text103,Text104,Text074,Text062,Text029,Text023,Text035,Text053,Text037,Text004,Text028,Text085,Text086,Text017,Text001,Text146,Text145,Text147,Text150,Text148,Text009,Text016,Text038,Text025,Text092,Text093,+561 more]
FEATURE [Part::Feature] Edge
  shape: bbox 2385 x 10100 x 2e-07 mm, 0 faces, 0 solids (baked)
FEATURE [Part::Feature] Edge001
  shape: bbox 1086 x 6907 x 2e-07 mm, 0 faces, 0 solids (baked)
FEATURE [Part::Feature] Edge002
  shape: bbox 5802 x 1529 x 2e-07 mm, 0 faces, 0 solids (baked)
FEATURE [Part::Feature] Edge003
  shape: bbox 7344 x 1734 x 2e-07 mm, 0 faces, 0 solids (baked)
FEATURE [Part::Feature] Edge004
  shape: bbox 6814 x 1603 x 2e-07 mm, 0 faces, 0 solids (baked)
FEATURE [Part::Feature] Edge005
  shape: bbox 9774 x 1536 x 2e-07 mm, 0 faces, 0 solids (baked)
FEATURE [Part::Feature] Edge006
  shape: bbox 8122 x 1563 x 2e-07 mm, 0 faces, 0 solids (baked)
FEATURE [Part::Feature] Edge007
  shape: bbox 1607 x 6805 x 2e-07 mm, 0 faces, 0 solids (baked)
FEATURE [Part::Feature] Edge008
  shape: bbox 1360 x 5781 x 2e-07 mm, 0 faces, 0 solids (baked)
FEATURE [Part::Feature] Edge010
  shape: bbox 634.1 x 329.4 x 2e-07 mm, 0 faces, 0 solids (baked)
FEATURE [Part::Feature] Edge012
  shape: bbox 5803 x 1528 x 2e-07 mm, 0 faces, 0 solids (baked)
FEATURE [Part::Feature] Edge013
  shape: bbox 5792 x 1565 x 2e-07 mm, 0 faces, 0 solids (baked)
FEATURE [Part::Feature] Edge026
  shape: bbox 6952 x 819.5 x 2e-07 mm, 0 faces, 0 solids (baked)
FEATURE [Part::Feature] Edge027
  shape: bbox 16110 x 6200 x 2e-07 mm, 0 faces, 0 solids (baked)
FEATURE [Part::Feature] Edge028
  shape: bbox 1469 x 12460 x 2e-07 mm, 0 faces, 0 solids (baked)
FEATURE [Part::Feature] Edge029
  shape: bbox 12500 x 2858 x 2e-07 mm, 0 faces, 0 solids (baked)
FEATURE [Part::Feature] Edge030
  shape: bbox 3072 x 1471 x 2e-07 mm, 0 faces, 0 solids (baked)
FEATURE [Part::Feature] Edge031
  shape: bbox 7027 x 3877 x 2e-07 mm, 0 faces, 0 solids (baked)
FEATURE [Part::Feature] Edge032
  shape: bbox 10110 x 4758 x 2e-07 mm, 0 faces, 0 solids (baked)
FEATURE [Part::Feature] Edge033
  shape: bbox 3548 x 9794 x 2e-07 mm, 0 faces, 0 solids (baked)
FEATURE [Part::Feature] Edge034
  shape: bbox 4015 x 8529 x 2e-07 mm, 0 faces, 0 solids (baked)
FEATURE [Part::Feature] Edge035
  shape: bbox 4347 x 7880 x 2e-07 mm, 0 faces, 0 solids (baked)
FEATURE [Part::Feature] Edge036
  shape: bbox 1549 x 4023 x 2e-07 mm, 0 faces, 0 solids (baked)
FEATURE [Part::Feature] Edge037
  shape: bbox 1962 x 5329 x 2e-07 mm, 0 faces, 0 solids (baked)
FEATURE [Part::Feature] Edge038
  shape: bbox 15130 x 6811 x 2e-07 mm, 0 faces, 0 solids (baked)
FEATURE [Part::Feature] Edge039
  shape: bbox 11310 x 5144 x 2e-07 mm, 0 faces, 0 solids (baked)
FEATURE [Part::Feature] Edge040
  shape: bbox 4485 x 9963 x 2e-07 mm, 0 faces, 0 solids (baked)
FEATURE [Part::Feature] Edge041
  shape: bbox 5700 x 1259 x 2e-07 mm, 0 faces, 0 solids (baked)
FEATURE [Part::Feature] Edge042
  shape: bbox 2897 x 6373 x 2e-07 mm, 0 faces, 0 solids (baked)
FEATURE [Part::Feature] Edge043
  shape: bbox 5605 x 2143 x 2e-07 mm, 0 faces, 0 solids (baked)
FEATURE [Part::Feature] Edge044
  shape: bbox 4669 x 3769 x 2e-07 mm, 0 faces, 0 solids (baked)
FEATURE [Part::Feature] Edge045
  shape: bbox 9577 x 106.6 x 2e-07 mm, 0 faces, 0 solids (baked)
FEATURE [Part::Feature] Edge046
  shape: bbox 7410 x 9179 x 2e-07 mm, 0 faces, 0 solids (baked)
FEATURE [Part::Feature] Edge047
  shape: bbox 6182 x 16170 x 2e-07 mm, 0 faces, 0 solids (baked)
FEATURE [Part::Feature] Edge048
  shape: bbox 2745 x 10160 x 2e-07 mm, 0 faces, 0 solids (baked)
FEATURE [Part::Feature] Edge049
  shape: bbox 3736 x 14180 x 2e-07 mm, 0 faces, 0 solids (baked)
FEATURE [Part::Feature] Edge050
  shape: bbox 2564 x 9809 x 2e-07 mm, 0 faces, 0 solids (baked)
FEATURE [Part::Feature] Edge051
  shape: bbox 1413 x 1730 x 2e-07 mm, 0 faces, 0 solids (baked)
FEATURE [Part::Feature] Edge052
  shape: bbox 10640 x 408.6 x 2e-07 mm, 0 faces, 0 solids (baked)
FEATURE [Part::Feature] Edge053
  shape: bbox 3094 x 6833 x 2e-07 mm, 0 faces, 0 solids (baked)
FEATURE [Part::Feature] Edge054
  shape: bbox 4990 x 313.3 x 2e-07 mm, 0 faces, 0 solids (baked)
FEATURE [Part::Feature] Edge055
  shape: bbox 3493 x 7679 x 2e-07 mm, 0 faces, 0 solids (baked)
FEATURE [Part::Feature] Edge056
  shape: bbox 3552 x 7845 x 2e-07 mm, 0 faces, 0 solids (baked)
FEATURE [Part::Feature] Edge057
  shape: bbox 16240 x 2919 x 2e-07 mm, 0 faces, 0 solids (baked)
FEATURE [Part::Feature] Edge058
  shape: bbox 113.4 x 1487 x 2e-07 mm, 0 faces, 0 solids (baked)
FEATURE [Part::Feature] Edge059
  shape: bbox 600 x 9558 x 2e-07 mm, 0 faces, 0 solids (baked)
FEATURE [Part::Feature] Edge060
  shape: bbox 1610 x 186.6 x 2e-07 mm, 0 faces, 0 solids (baked)
FEATURE [Part::Feature] Edge061
  shape: bbox 722.9 x 15880 x 2e-07 mm, 0 faces, 0 solids (baked)
FEATURE [Part::Feature] Edge062
  shape: bbox 10470 x 671 x 2e-07 mm, 0 faces, 0 solids (baked)
FEATURE [Part::Feature] Edge063
  shape: bbox 10770 x 687.6 x 2e-07 mm, 0 faces, 0 solids (baked)
FEATURE [Part::Feature] Edge064
  shape: bbox 100.1 x 6.481 x 2e-07 mm, 0 faces, 0 solids (baked)
FEATURE [Part::Feature] Edge065
  shape: bbox 5738 x 1482 x 2e-07 mm, 0 faces, 0 solids (baked)
FEATURE [Part::Feature] Edge066
  shape: bbox 623.7 x 7481 x 2e-07 mm, 0 faces, 0 solids (baked)
FEATURE [Part::Feature] Edge067
  shape: bbox 414.6 x 6224 x 2e-07 mm, 0 faces, 0 solids (baked)
FEATURE [Part::Feature] Edge068
  shape: bbox 4818 x 833.2 x 2e-07 mm, 0 faces, 0 solids (baked)
FEATURE [Part::Feature] Edge069
  shape: bbox 1400 x 41.25 x 2e-07 mm, 0 faces, 0 solids (baked)
FEATURE [Part::Feature] Edge070
  shape: bbox 143.2 x 4818 x 2e-07 mm, 0 faces, 0 solids (baked)
FEATURE [Part::Feature] Edge071
  shape: bbox 5417 x 417.8 x 2e-07 mm, 0 faces, 0 solids (baked)
FEATURE [Part::Feature] Edge072
  shape: bbox 104.4 x 4296 x 2e-07 mm, 0 faces, 0 solids (baked)
FEATURE [Part::Feature] Edge073
  shape: bbox 1234 x 145.5 x 2e-07 mm, 0 faces, 0 solids (baked)
FEATURE [Part::Feature] Edge074
  shape: bbox 286.3 x 5515 x 2e-07 mm, 0 faces, 0 solids (baked)
FEATURE [Part::Feature] Edge075
  shape: bbox 348.2 x 7368 x 2e-07 mm, 0 faces, 0 solids (baked)
FEATURE [Part::Feature] Edge076
  shape: bbox 9577 x 92.62 x 2e-07 mm, 0 faces, 0 solids (baked)
FEATURE [Part::Feature] Edge077
  shape: bbox 2457 x 9569 x 2e-07 mm, 0 faces, 0 solids (baked)
FEATURE [Part::Feature] Edge078
  shape: bbox 9577 x 92.62 x 2e-07 mm, 0 faces, 0 solids (baked)
FEATURE [Part::Feature] Edge079
  shape: bbox 1880 x 53.56 x 2e-07 mm, 0 faces, 0 solids (baked)
FEATURE [Part::Feature] Edge080
  shape: bbox 183.7 x 19120 x 2e-07 mm, 0 faces, 0 solids (baked)
FEATURE [Part::Feature] Edge081
  shape: bbox 75.03 x 7968 x 2e-07 mm, 0 faces, 0 solids (baked)
FEATURE [Part::Feature] Edge082
  shape: bbox 230.9 x 20820 x 2e-07 mm, 0 faces, 0 solids (baked)
FEATURE [Part::Feature] Edge083
  shape: bbox 1876 x 2321 x 2e-07 mm, 0 faces, 0 solids (baked)
FEATURE [Part::Feature] Edge084
  shape: bbox 7040 x 1250 x 2e-07 mm, 0 faces, 0 solids (baked)
FEATURE [Part::Feature] Edge085
  shape: bbox 425.9 x 1659 x 2e-07 mm, 0 faces, 0 solids (baked)
FEATURE [Part::Feature] Edge086
  shape: bbox 5893 x 1048 x 2e-07 mm, 0 faces, 0 solids (baked)
FEATURE [Part::Feature] Edge087
  shape: bbox 4815 x 6080 x 2e-07 mm, 0 faces, 0 solids (baked)
FEATURE [Part::Feature] Edge088
  shape: bbox 302.3 x 7493 x 2e-07 mm, 0 faces, 0 solids (baked)
FEATURE [Part::Feature] Edge089
  shape: bbox 3173 x 195.8 x 2e-07 mm, 0 faces, 0 solids (baked)
FEATURE [Part::Feature] Edge090
  shape: bbox 15790 x 3866 x 2e-07 mm, 0 faces, 0 solids (baked)
FEATURE [Part::Feature] Edge091
  shape: bbox 3738 x 8260 x 2e-07 mm, 0 faces, 0 solids (baked)
FEATURE [Part::Feature] Edge092
  shape: bbox 15780 x 3931 x 2e-07 mm, 0 faces, 0 solids (baked)
FEATURE [Part::Feature] Edge093
  shape: bbox 641.6 x 12410 x 2e-07 mm, 0 faces, 0 solids (baked)
FEATURE [Part::Feature] Edge094
  shape: bbox 12060 x 571.4 x 2e-07 mm, 0 faces, 0 solids (baked)
FEATURE [Part::Feature] Edge095
  shape: bbox 48.76 x 740.8 x 2e-07 mm, 0 faces, 0 solids (baked)
FEATURE [Part::Feature] Edge096
  shape: bbox 1864 x 271.7 x 2e-07 mm, 0 faces, 0 solids (baked)
FEATURE [Part::Feature] Edge097
  shape: bbox 80.56 x 843.7 x 2e-07 mm, 0 faces, 0 solids (baked)
FEATURE [Part::Feature] Edge098
  shape: bbox 1620 x 154.8 x 2e-07 mm, 0 faces, 0 solids (baked)
FEATURE [Part::Feature] Edge099
  shape: bbox 80.67 x 843.2 x 2e-07 mm, 0 faces, 0 solids (baked)
FEATURE [Part::Feature] Edge100
  shape: bbox 54.17 x 647.9 x 2e-07 mm, 0 faces, 0 solids (baked)
FEATURE [Part::Feature] Edge101
  shape: bbox 51.63 x 617.9 x 2e-07 mm, 0 faces, 0 solids (baked)
FEATURE [Part::Feature] Edge102
  shape: bbox 1508 x 127.1 x 2e-07 mm, 0 faces, 0 solids (baked)
FEATURE [Part::Feature] Edge103
  shape: bbox 33.68 x 745.6 x 2e-07 mm, 0 faces, 0 solids (baked)
FEATURE [Part::Feature] Edge104
  shape: bbox 32.14 x 715.6 x 2e-07 mm, 0 faces, 0 solids (baked)
FEATURE [Part::Feature] Edge105
  shape: bbox 1512 x 68.05 x 2e-07 mm, 0 faces, 0 solids (baked)
FEATURE [Part::Feature] Edge106
  shape: bbox 14490 x 1380 x 2e-07 mm, 0 faces, 0 solids (baked)
FEATURE [Part::Feature] Edge107
  shape: bbox 1500 x 149.1 x 2e-07 mm, 0 faces, 0 solids (baked)
FEATURE [Part::Feature] Edge108
  shape: bbox 6638 x 459.3 x 2e-07 mm, 0 faces, 0 solids (baked)
FEATURE [Part::Feature] Edge109
  shape: bbox 38.02 x 791.5 x 2e-07 mm, 0 faces, 0 solids (baked)
FEATURE [Part::Feature] Edge110
  shape: bbox 638.4 x 18.31 x 2e-07 mm, 0 faces, 0 solids (baked)
FEATURE [Part::Feature] Edge111
  shape: bbox 5229 x 885.5 x 2e-07 mm, 0 faces, 0 solids (baked)
FEATURE [Part::Feature] Edge112
  shape: bbox 15290 x 8235 x 2e-07 mm, 0 faces, 0 solids (baked)
FEATURE [Part::Feature] Edge113
  shape: bbox 1437 x 2554 x 2e-07 mm, 0 faces, 0 solids (baked)
FEATURE [Part::Feature] Edge114
  shape: bbox 4295 x 19450 x 2e-07 mm, 0 faces, 0 solids (baked)
FEATURE [Part::Feature] Edge115
  shape: bbox 6595 x 29890 x 2e-07 mm, 0 faces, 0 solids (baked)
FEATURE [Part::Feature] Edge116
  shape: bbox 127.5 x 362.1 x 2e-07 mm, 0 faces, 0 solids (baked)
FEATURE [Part::Feature] Edge117
  shape: bbox 179.2 x 342.3 x 2e-07 mm, 0 faces, 0 solids (baked)
FEATURE [Part::Feature] Edge118
  shape: bbox 226.8 x 313.6 x 2e-07 mm, 0 faces, 0 solids (baked)
FEATURE [Part::Feature] Edge119
  shape: bbox 269.2 x 275.9 x 2e-07 mm, 0 faces, 0 solids (baked)
FEATURE [Part::Feature] Edge120
  shape: bbox 235.6 x 168.4 x 2e-07 mm, 0 faces, 0 solids (baked)
FEATURE [Part::Feature] Edge121
  shape: bbox 268.9 x 120.9 x 2e-07 mm, 0 faces, 0 solids (baked)
FEATURE [Part::Feature] Edge122
  shape: bbox 287.1 x 68.65 x 2e-07 mm, 0 faces, 0 solids (baked)
FEATURE [Part::Feature] Edge123
  shape: bbox 290.2 x 12.6 x 2e-07 mm, 0 faces, 0 solids (baked)
FEATURE [Part::Feature] Edge124
  shape: bbox 9991 x 480.4 x 2e-07 mm, 0 faces, 0 solids (baked)
FEATURE [Part::Feature] Edge125
  shape: bbox 134.3 x 2876 x 2e-07 mm, 0 faces, 0 solids (baked)
FEATURE [Part::Feature] Edge126
  shape: bbox 24830 x 637.1 x 2e-07 mm, 0 faces, 0 solids (baked)
FEATURE [Part::Feature] Edge127
  shape: bbox 122.4 x 15900 x 2e-07 mm, 0 faces, 0 solids (baked)
FEATURE [Part::Feature] Edge128
  shape: bbox 10050 x 608.4 x 2e-07 mm, 0 faces, 0 solids (baked)
FEATURE [Part::Feature] Edge129
  shape: bbox 7019 x 283.5 x 2e-07 mm, 0 faces, 0 solids (baked)
FEATURE [Part::Feature] Edge130
  shape: bbox 157.8 x 3376 x 2e-07 mm, 0 faces, 0 solids (baked)
FEATURE [Part::Feature] Edge131
  shape: bbox 23.42 x 499.4 x 2e-07 mm, 0 faces, 0 solids (baked)
FEATURE [Part::Feature] Edge132
  shape: bbox 121.3 x 15890 x 2e-07 mm, 0 faces, 0 solids (baked)
FEATURE [Part::Feature] Edge133
  shape: bbox 21910 x 1424 x 2e-07 mm, 0 faces, 0 solids (baked)
FEATURE [Part::Feature] Edge134
  shape: bbox 23.42 x 499.4 x 2e-07 mm, 0 faces, 0 solids (baked)
FEATURE [Part::Feature] Edge135
  shape: bbox 5037 x 235.6 x 2e-07 mm, 0 faces, 0 solids (baked)
FEATURE [Part::Feature] Edge136
  shape: bbox 737.3 x 15490 x 2e-07 mm, 0 faces, 0 solids (baked)
FEATURE [Part::Feature] Edge137
  shape: bbox 933.5 x 26.83 x 2e-07 mm, 0 faces, 0 solids (baked)
FEATURE [Part::Feature] Edge138
  shape: bbox 11990 x 2859 x 2e-07 mm, 0 faces, 0 solids (baked)
FEATURE [Part::Feature] Edge139
  shape: bbox 2481 x 10400 x 2e-07 mm, 0 faces, 0 solids (baked)
FEATURE [Part::Feature] Edge140
  shape: bbox 12290 x 986.7 x 2e-07 mm, 0 faces, 0 solids (baked)
FEATURE [Part::Feature] Edge141
  shape: bbox 60.1 x 4563 x 2e-07 mm, 0 faces, 0 solids (baked)
FEATURE [Part::Feature] Edge142
  shape: bbox 169.8 x 8.579 x 2e-07 mm, 0 faces, 0 solids (baked)
FEATURE [Part::Feature] Edge143
  shape: bbox 12830 x 3327 x 2e-07 mm, 0 faces, 0 solids (baked)
FEATURE [Part::Feature] Edge144
  shape: bbox 1298 x 418.4 x 2e-07 mm, 0 faces, 0 solids (baked)
FEATURE [Part::Feature] Edge145
  shape: bbox 191.4 x 896.4 x 2e-07 mm, 0 faces, 0 solids (baked)
FEATURE [Part::Feature] Edge150
  shape: bbox 78.83 x 793 x 2e-07 mm, 0 faces, 0 solids (baked)
FEATURE [Part::Feature] Edge151
  shape: bbox 75.58 x 793.6 x 2e-07 mm, 0 faces, 0 solids (baked)
FEATURE [Part::Feature] Edge152
  shape: bbox 1646 x 481 x 2e-07 mm, 0 faces, 0 solids (baked)
FEATURE [Part::Feature] Edge154
  shape: bbox 3813 x 164.8 x 2e-07 mm, 0 faces, 0 solids (baked)
FEATURE [Part::Feature] Edge155
  shape: bbox 612 x 7741 x 2e-07 mm, 0 faces, 0 solids (baked)
FEATURE [Part::Feature] Edge156
  shape: bbox 120.5 x 1368 x 2e-07 mm, 0 faces, 0 solids (baked)
FEATURE [Part::Feature] Wire
  shape: bbox 24000 x 27010 x 2e-07 mm, 0 faces, 0 solids (baked)
FEATURE [Part::Extrusion] Extrude
  Base = -> Wire
  Dir = (0,0,8500)
  Placement = pos=(0,0,26225) rot=(0,0,1;0rad)
  Solid = true
FEATURE [Part::Part2DObjectPython] DWire  # Draft 2D object (typed FeaturePython)
  ChamferSize = 0
  Closed = true
  End = (-9.74853e+07,-6.33588e+07,0)
  FilletRadius = 0
  Length = 49453.9
  MakeFace = true
  Points = (4) [(-97488900,-63351100,0),(-97473100,-63347200,0),(-97469600,-63354900,0),(-97485300,-63358800,0)]
  Start = (-9.74889e+07,-6.33511e+07,0)
  Subdivisions = 0
FEATURE [Part::Extrusion] Extrude001
  Base = -> DWire
  Dir = (0,0,8430)
  Solid = true
FEATURE [Part::Part2DObjectPython] DWire001  # Draft 2D object (typed FeaturePython)
  ChamferSize = 0
  Closed = true
  End = (-9.7466e+07,-6.33627e+07,0)
  FilletRadius = 0
  Length = 54110.6
  MakeFace = true
  Points = (6) [(-97469600,-63354900,0),(-97485300,-63358800,0),(-97484900,-63367300,0),(-97482100,-63367100,0),(-97482300,-63365600,0),(-97466000,-63362700,0)]
  Start = (-9.74696e+07,-6.33549e+07,0)
  Subdivisions = 0
FEATURE [Part::Extrusion] Extrude002
  Base = -> DWire001
  Dir = (0,0,7750)
  Solid = true
FEATURE [Part::Part2DObjectPython] Line  # Draft 2D object (typed FeaturePython)
  ChamferSize = 0
  Closed = false
  End = (-9.74731e+07,-6.33472e+07,0)
  FilletRadius = 0
  Length = 24244
  MakeFace = true
  Points = (2) [(-97496600,-63353000,0),(-97473100,-63347200,0)]
  Start = (-9.74966e+07,-6.3353e+07,0)
  Subdivisions = 0
FEATURE [Part::Part2DObjectPython] DWire002  # Draft 2D object (typed FeaturePython)
  ChamferSize = 0
  Closed = true
  End = (-97484872,-63367292,0)
  FilletRadius = 0
  Length = 36959.4
  MakeFace = true
  Points = (7) [(-97485300,-63358800,0),(-97495400,-63359500,0),(-97495900,-63365700,0),(-97491000,-63366600,0),(-97489600,-63366600,0),(-97489700,-63367600,0),+1 more]
  Start = (-97485344,-63358800,0)
  Subdivisions = 0
FEATURE [Part::Extrusion] Extrude003
  Base = -> DWire002
  Dir = (0,0,6520)
  Solid = true
FEATURE [Part::Part2DObjectPython] DWire003  # Draft 2D object (typed FeaturePython)
  ChamferSize = 0
  Closed = true
  End = (-97489672,-63367592,0)
  FilletRadius = 0
  Length = 45697.6
  MakeFace = true
  Points = (10) [(-97482100,-63367100,0),(-97481500,-63376700,0),(-97483100,-63376900,0),(-97493900,-63377600,0),(-97494900,-63377600,0),(-97494900,-63376100,0),+4 more]
  Start = (-9.74821e+07,-6.33671e+07,0)
  Subdivisions = 0
FEATURE [Part::Extrusion] Extrude004
  Base = -> DWire003
  Dir = (0,0,6170)
  Solid = true
FEATURE [Part::Part2DObjectPython] DWire004  # Draft 2D object (typed FeaturePython)
  ChamferSize = 0
  Closed = true
  End = (-97485344,-63358800,0)
  FilletRadius = 0
  Length = 31816.6
  MakeFace = true
  Points = (4) [(-97488900,-63351100,0),(-97494900,-63352500,0),(-97495400,-63359500,0),(-97485300,-63358800,0)]
  Start = (-9.74889e+07,-6.33511e+07,0)
  Subdivisions = 0
FEATURE [Part::Extrusion] Extrude005
  Base = -> DWire004
  Dir = (0,0,4000)
  Solid = true
FEATURE [Part::Part2DObjectPython] DWire005  # Draft 2D object (typed FeaturePython)
  ChamferSize = 0
  Closed = true
  End = (-97494912,-63377564,0)
  FilletRadius = 0
  Length = 55546.6
  MakeFace = true
  Points = (8) [(-97483100,-63376900,0),(-97482400,-63392700,0),(-97492900,-63393400,0),(-97493200,-63386100,0),(-97493300,-63386100,0),(-97493600,-63380500,0),+2 more]
  Start = (-9.74831e+07,-6.33769e+07,0)
  Subdivisions = 0
FEATURE [Part::Extrusion] Extrude006
  Base = -> DWire005
  Dir = (0,0,7300)
  Solid = true
FEATURE [Part::Part2DObjectPython] DWire006  # Draft 2D object (typed FeaturePython)
  ChamferSize = 0
  Closed = true
  End = (-9.75005e+07,-6.3386e+07,0)
  FilletRadius = 0
  Length = 35123.7
  MakeFace = true
  Points = (5) [(-97496700,-63385900,0),(-97496100,-63393600,0),(-97506100,-63394200,0),(-97506400,-63386700,0),(-97500500,-63386000,0)]
  Start = (-9.74967e+07,-6.33859e+07,0)
  Subdivisions = 0
FEATURE [Part::Extrusion] Extrude007
  Base = -> DWire006
  Dir = (0,0,7100)
  Solid = true
FEATURE [Part::Part2DObjectPython] DWire008  label="DWire007"  # Draft 2D object (typed FeaturePython)
  ChamferSize = 0
  Closed = true
  End = (-9.75063e+07,-6.33897e+07,0)
  FilletRadius = 0
  Length = 23139.5
  MakeFace = true
  Points = (6) [(-97506100,-63394200,0),(-97513100,-63394500,0),(-97513300,-63391100,0),(-97511400,-63391000,0),(-97511400,-63389900,0),(-97506300,-63389700,0)]
  Start = (-9.75061e+07,-6.33942e+07,0)
  Subdivisions = 0
FEATURE [Part::Extrusion] Extrude008
  Base = -> DWire008
  Dir = (0,0,2760)
  Solid = true
FEATURE [Part::Part2DObjectPython] Line001  # Draft 2D object (typed FeaturePython)
  ChamferSize = 0
  Closed = false
  End = (-9.75114e+07,-6.3391e+07,0)
  FilletRadius = 0
  Length = 15572.9
  MakeFace = true
  Points = (2) [(-97511900,-63375400,0),(-97511400,-63391000,0)]
  Start = (-9.75119e+07,-6.33754e+07,0)
  Subdivisions = 0
FEATURE [Part::Part2DObjectPython] Line003  # Draft 2D object (typed FeaturePython)
  ChamferSize = 0
  Closed = false
  End = (-9.7513e+07,-6.33764e+07,0)
  FilletRadius = 0
  Length = 835.873
  MakeFace = true
  Points = (2) [(-97513100,-63375600,0),(-97513000,-63376400,0)]
  Start = (-9.75131e+07,-6.33756e+07,0)
  Subdivisions = 0
FEATURE [Part::Part2DObjectPython] DWire009  # Draft 2D object (typed FeaturePython)
  ChamferSize = 0
  Closed = true
  End = (-9.7536e+07,-6.33776e+07,25930)
  FilletRadius = 0
  Length = 91887.2
  MakeFace = true
  Points = (29) [(-97537600,-63377700,25930),(-97538300,-63393200,25930),(-97533300,-63392900,25930),(-97533300,-63392400,25930),(-97528900,-63392100,25930),+24 more]
  Start = (-9.75376e+07,-6.33777e+07,25930)
  Subdivisions = 0
FEATURE [Part::Extrusion] Extrude009
  Base = -> DWire009
  Dir = (0,0,16500)
  Solid = true
FEATURE [Part::Part2DObjectPython] DWire010  # Draft 2D object (typed FeaturePython)
  ChamferSize = 0
  Closed = true
  End = (-9.75114e+07,-6.33899e+07,0)
  FilletRadius = 0
  Length = 43362.5
  MakeFace = true
  Points = (7) [(-97511400,-63389900,0),(-97506300,-63389700,0),(-97506400,-63386700,0),(-97500500,-63386000,0),(-97500900,-63378400,0),(-97511800,-63379100,0),+1 more]
  Start = (-97511416,-63389872,0)
  Subdivisions = 0
FEATURE [Part::Extrusion] Extrude010
  Base = -> DWire010
  Dir = (0,0,8820)
  Solid = true
FEATURE [Part::Part2DObjectPython] DWire011  # Draft 2D object (typed FeaturePython)
  ChamferSize = 0
  Closed = true
  End = (-9.75119e+07,-6.33763e+07,0)
  FilletRadius = 0
  Length = 33918.9
  MakeFace = true
  Points = (6) [(-97513000,-63376400,0),(-97513200,-63374200,0),(-97501100,-63373600,0),(-97500900,-63378400,0),(-97511800,-63379100,0),(-97511900,-63376300,0)]
  Start = (-9.7513e+07,-6.33764e+07,0)
  Subdivisions = 0
FEATURE [Part::Extrusion] Extrude011
  Base = -> DWire011
  Dir = (0,0,6000)
  Solid = true
FEATURE [Part::Part2DObjectPython] DWire012  # Draft 2D object (typed FeaturePython)
  ChamferSize = 0
  Closed = true
  End = (-9.75467e+07,-6.33443e+07,0)
  FilletRadius = 0
  Length = 63079.3
  MakeFace = true
  Points = (6) [(-97548200,-63332700,0),(-97532900,-63324500,0),(-97531500,-63327000,0),(-97535700,-63346500,0),(-97541400,-63345200,0),(-97546700,-63344300,0)]
  Start = (-9.75482e+07,-6.33327e+07,0)
  Subdivisions = 0
FEATURE [Part::Extrusion] Extrude012
  Base = -> DWire012
  Dir = (0,0,12500)
  Solid = true
FEATURE [Part::Part2DObjectPython] DWire013  # Draft 2D object (typed FeaturePython)
  ChamferSize = 0
  Closed = true
  End = (-9.75414e+07,-6.33452e+07,0)
  FilletRadius = 0
  Length = 89463.2
  MakeFace = true
  Points = (13) [(-97535700,-63346500,0),(-97542300,-63376400,0),(-97542500,-63376700,0),(-97542700,-63377100,0),(-97542900,-63377400,0),(-97543100,-63377700,0),+7 more]
  Start = (-9.75357e+07,-6.33465e+07,0)
  Subdivisions = 0
FEATURE [Part::Extrusion] Extrude013
  Base = -> DWire013
  Dir = (0,0,8300)
  Solid = true
FEATURE [Part::Part2DObjectPython] DWire014  # Draft 2D object (typed FeaturePython)
  ChamferSize = 0
  Closed = true
  End = (-9.75146e+07,-6.32975e+07,0)
  FilletRadius = 0
  Length = 41273.8
  MakeFace = true
  Points = (4) [(-97524300,-63301000,0),(-97520700,-63310700,0),(-97510600,-63306000,0),(-97514600,-63297500,0)]
  Start = (-9.75243e+07,-6.3301e+07,0)
  Subdivisions = 0
FEATURE [Part::Extrusion] Extrude014
  Base = -> DWire014
  Dir = (0,0,6750)
  Solid = true
FEATURE [Part::Part2DObjectPython] DWire015  # Draft 2D object (typed FeaturePython)
  ChamferSize = 0
  Closed = true
  End = (-9.75079e+07,-6.32942e+07,0)
  FilletRadius = 0
  Length = 33883.5
  MakeFace = true
  Points = (4) [(-97514600,-63297500,0),(-97510600,-63306000,0),(-97503600,-63302100,0),(-97507900,-63294200,0)]
  Start = (-9.75146e+07,-6.32975e+07,0)
  Subdivisions = 0
FEATURE [Part::Extrusion] Extrude015
  Base = -> DWire015
  Dir = (0,0,8000)
  Solid = true
FEATURE [Part::Part2DObjectPython] DWire016  # Draft 2D object (typed FeaturePython)
  ChamferSize = 0
  Closed = true
  End = (-9.75273e+07,-6.33043e+07,0)
  FilletRadius = 0
  Length = 54768.5
  MakeFace = true
  Points = (5) [(-97543400,-63310500,0),(-97539000,-63320500,0),(-97523800,-63313700,0),(-97525800,-63308300,0),(-97527300,-63304300,0)]
  Start = (-9.75434e+07,-6.33105e+07,0)
  Subdivisions = 0
FEATURE [Part::Extrusion] Extrude016
  Base = -> DWire016
  Dir = (0,0,8000)
  Solid = true
FEATURE [Part::Part2DObjectPython] DWire017  # Draft 2D object (typed FeaturePython)
  ChamferSize = 0
  Closed = true
  End = (-9.75023e+07,-6.32929e+07,0)
  FilletRadius = 0
  Length = 26109.7
  MakeFace = true
  Points = (4) [(-97507900,-63294200,0),(-97503600,-63302100,0),(-97500500,-63300600,0),(-97502300,-63292900,0)]
  Start = (-9.75079e+07,-6.32942e+07,0)
  Subdivisions = 0
FEATURE [Part::Extrusion] Extrude017
  Base = -> DWire017
  Dir = (0,0,11000)
  Solid = true
FEATURE [Part::Feature] Edge009
  shape: bbox 1762 x 7703 x 25000 mm, 0 faces, 0 solids (baked)
FEATURE [App::DocumentObjectGroup] Group002  label="construcoes"
  Group = -> [Edge,Edge005,Edge004,Edge013,Edge002,Edge008,Edge012,Edge001,Edge010,Edge006,Edge007,Edge003,Edge009,Edge044,Edge045,Edge046,Edge047,Edge048,Edge049,Edge050,Edge051,Edge052,Edge053,Edge054,Edge055,Edge056,Edge057,Edge058,Edge073,Edge059,Edge060,Edge061,Edge062,Edge063,Edge064,Edge065,Edge066,Edge067,Edge068,Edge069,Edge070,Edge071,Edge072,Edge089,Edge074,Edge075,Edge076,Edge077,Edge078,Edge079,+89 more]
FEATURE [App::DocumentObjectGroup] Group001  label="levantamento"
  Group = -> [ENTITIES_pontos,ENTITIES_CAIXAS_DE_VISITA,ENTITIES_CAIXAS_DIVERSAS_ELECT_E_TELEC__,ENTITIES_DEGRAUS,ENTITIES_ESTACIONAMENTOS,ENTITIES_ESTACOES,ENTITIES_HATCH,ENTITIES_PINOS,ENTITIES_RAMPA,ENTITIES_MUROS,ENTITIES_LANCIS,ENTITIES_MALHA_DE_COORDENADAS,ENTITIES_SUMIDOUROS,ENTITIES_TALUDES,ENTITIES_TOPONIMIA,ENTITIES_VEDA__ES,ENTITIES_ZIGUEZAGUES,ENTITIES___REA_INTERVEN__O,Group002]
FEATURE [Part::Part2DObjectPython] DWire019  # Draft 2D object (typed FeaturePython)
  ChamferSize = 0
  Closed = true
  End = (-9.75023e+07,-6.32929e+07,0)
  FilletRadius = 0
  Length = 22647
  MakeFace = true
  Points = (4) [(-97500500,-63300600,0),(-97497200,-63299900,0),(-97498900,-63292200,0),(-97502300,-63292900,0)]
  Start = (-9.75005e+07,-6.33006e+07,0)
  Subdivisions = 0
FEATURE [Part::Extrusion] Extrude018
  Base = -> DWire019
  Dir = (0,0,13500)
  Solid = true
FEATURE [Part::Part2DObjectPython] DWire020  # Draft 2D object (typed FeaturePython)
  ChamferSize = 0
  Closed = true
  End = (-9.74964e+07,-6.32861e+07,0)
  FilletRadius = 0
  Length = 43333
  MakeFace = true
  Points = (5) [(-97498900,-63292200,0),(-97497200,-63299900,0),(-97488000,-63297800,0),(-97489500,-63285300,0),(-97496400,-63286100,0)]
  Start = (-9.74989e+07,-6.32922e+07,0)
  Subdivisions = 0
FEATURE [Part::Extrusion] Extrusion
  Base = -> DWire020
  Dir = (0,0,10950)
  Solid = true
FEATURE [Part::Part2DObjectPython] DWire021  # Draft 2D object (typed FeaturePython)
  ChamferSize = 0
  Closed = true
  End = (-9.74768e+07,-6.32896e+07,0)
  FilletRadius = 0
  Length = 33189.6
  MakeFace = true
  Points = (4) [(-97484100,-63291300,0),(-97482500,-63298100,0),(-97474400,-63299700,0),(-97476800,-63289600,0)]
  Start = (-9.74841e+07,-6.32913e+07,0)
  Subdivisions = 0
FEATURE [Part::Part2DObjectPython] DWire022  # Draft 2D object (typed FeaturePython)
  ChamferSize = 0
  Closed = true
  End = (-9.74635e+07,-6.32943e+07,0)
  FilletRadius = 0
  Length = 41331.1
  MakeFace = true
  Points = (4) [(-97476800,-63289600,0),(-97474400,-63299700,0),(-97464600,-63301200,0),(-97463500,-63294300,0)]
  Start = (-9.74768e+07,-6.32896e+07,0)
  Subdivisions = 0
FEATURE [Part::Part2DObjectPython] DWire023  # Draft 2D object (typed FeaturePython)
  ChamferSize = 0
  Closed = true
  End = (-9.74768e+07,-6.32896e+07,34800)
  FilletRadius = 0
  Length = 37987.8
  MakeFace = true
  Points = (4) [(-97474900,-63297600,34800),(-97464300,-63299300,34800),(-97463500,-63294300,34800),(-97476800,-63289600,34800)]
  Start = (-9.74749e+07,-6.32976e+07,34800)
  Subdivisions = 0
FEATURE [Part::Extrusion] Extrusion001
  Base = -> DWire021
  Dir = (0,0,10950)
  Solid = true
FEATURE [Part::Extrusion] Extrusion002
  Base = -> DWire022
  Dir = (0,0,8800)
  Solid = true
FEATURE [Part::Extrusion] Extrude019
  Base = -> DWire023
  Dir = (0,0,3000)
  Solid = true
FEATURE [Part::Compound] Compound
  Links = -> [Extrude019,Extrusion002]
FEATURE [Part::Part2DObjectPython] DWire024  # Draft 2D object (typed FeaturePython)
  ChamferSize = 0
  Closed = true
  End = (-9.74715e+07,-6.33159e+07,0)
  FilletRadius = 0
  Length = 39302.5
  MakeFace = true
  Points = (5) [(-97467800,-63306300,0),(-97478400,-63305900,0),(-97479800,-63307600,0),(-97477300,-63317400,0),(-97471500,-63315900,0)]
  Start = (-9.74678e+07,-6.33063e+07,0)
  Subdivisions = 0
FEATURE [Part::Extrusion] Extrude020
  Base = -> DWire024
  Dir = (0,0,11000)
  Solid = true
FEATURE [Part::Part2DObjectPython] DWire025  # Draft 2D object (typed FeaturePython)
  ChamferSize = 0
  Closed = true
  End = (-9.74735e+07,-6.33316e+07,0)
  FilletRadius = 0
  Length = 41327.9
  MakeFace = true
  Points = (4) [(-97477300,-63317400,0),(-97471500,-63315900,0),(-97467700,-63330100,0),(-97473500,-63331600,0)]
  Start = (-9.74773e+07,-6.33174e+07,0)
  Subdivisions = 0
FEATURE [Part::Extrusion] Extrusion003
  Base = -> DWire025
  Dir = (0,0,10000)
  Solid = true
FEATURE [Part::Part2DObjectPython] DWire026  # Draft 2D object (typed FeaturePython)
  ChamferSize = 0
  Closed = true
  End = (-9.74677e+07,-6.33301e+07,26710)
  FilletRadius = 0
  Length = 33015.7
  MakeFace = true
  Points = (4) [(-97473500,-63331600,26710),(-97470800,-63341800,26710),(-97465000,-63340200,26710),(-97467700,-63330100,26710)]
  Start = (-9.74735e+07,-6.33316e+07,26710)
  Subdivisions = 0
FEATURE [Part::Extrusion] Extrusion004
  Base = -> DWire026
  Dir = (0,0,9680)
  Solid = true
FEATURE [Part::Part2DObjectPython] DWire028  label="DWire027"  # Draft 2D object (typed FeaturePython)
  ChamferSize = 0
  Closed = true
  End = (-9.7465e+07,-6.33402e+07,25000)
  FilletRadius = 0
  Length = 46015.1
  MakeFace = true
  Points = (4) [(-97470800,-63341800,25000),(-97464600,-63358000,25000),(-97459000,-63355800,25000),(-97465000,-63340200,25000)]
  Start = (-9.74708e+07,-6.33418e+07,25000)
  Subdivisions = 0
FEATURE [Part::Extrusion] Extrusion005
  Base = -> DWire028
  Dir = (0,0,9680)
  Solid = true
FEATURE [Part::Part2DObjectPython] DWire029  # Draft 2D object (typed FeaturePython)
  ChamferSize = 0
  Closed = true
  End = (-9.7459e+07,-6.33558e+07,26710)
  FilletRadius = 0
  Length = 33744.3
  MakeFace = true
  Points = (4) [(-97464600,-63358000,26710),(-97457200,-63367100,26710),(-97452500,-63363400,26710),(-97459000,-63355800,26710)]
  Start = (-9.74646e+07,-6.3358e+07,26710)
  Subdivisions = 0
FEATURE [Part::Extrusion] Extrusion006
  Base = -> DWire029
  Dir = (0,0,9680)
  Solid = true
FEATURE [Part::Part2DObjectPython] DWire030  label="25.75"  # Draft 2D object (typed FeaturePython)
  ChamferSize = 0
  Closed = true
  End = (-9.75358e+07,-6.33664e+07,0)
  FilletRadius = 0
  Length = 9292.31
  MakeFace = false
  Points = (6) [(-97536400,-63365700,0),(-97538900,-63365500,0),(-97539100,-63366600,0),(-97537500,-63368000,0),(-97536000,-63367400,0),(-97535800,-63366400,0)]
  Start = (-9.75364e+07,-6.33657e+07,0)
  Subdivisions = 0
FEATURE [Part::Part2DObjectPython] DWire031  label="25.5"  # Draft 2D object (typed FeaturePython)
  ChamferSize = 0
  Closed = true
  End = (-97520712,-63310748,25500)
  FilletRadius = 0
  Length = 6030.12
  MakeFace = false
  Points = (12) [(-97519900,-63310400,25500),(-97519600,-63310700,25500),(-97520000,-63310800,25500),(-97520400,-63311100,25500),(-97521100,-63311000,25500),+7 more]
  Start = (-9.75199e+07,-6.33104e+07,25500)
  Subdivisions = 0
FEATURE [Part::Part2DObjectPython] DWire032  label="25.076"  # Draft 2D object (typed FeaturePython)
  ChamferSize = 0
  Closed = true
  End = (-9.75441e+07,-6.33789e+07,0)
  FilletRadius = 0
  Length = 15989
  MakeFace = false
  Points = (9) [(-97542700,-63378600,0),(-97541800,-63377800,0),(-97540600,-63378500,0),(-97539800,-63379300,0),(-97539300,-63379500,0),(-97539300,-63379600,0),+3 more]
  Start = (-9.75427e+07,-6.33786e+07,0)
  Subdivisions = 0
FEATURE [Part::Part2DObjectPython] DWire033  label="25.077"  # Draft 2D object (typed FeaturePython)
  ChamferSize = 0
  Closed = true
  End = (-9.7539e+07,-6.33211e+07,0)
  FilletRadius = 0
  Length = 2396.37
  MakeFace = false
  Points = (4) [(-97538900,-63321700,0),(-97539800,-63321700,0),(-97539300,-63321100,0),(-97539000,-63321100,0)]
  Start = (-9.75389e+07,-6.33217e+07,0)
  Subdivisions = 0
FEATURE [Part::Part2DObjectPython] DWire034  label="25.078"  # Draft 2D object (typed FeaturePython)
  ChamferSize = 0
  Closed = true
  End = (-9.75264e+07,-6.33148e+07,0)
  FilletRadius = 0
  Length = 1510.71
  MakeFace = false
  Points = (3) [(-97527000,-63315100,0),(-97526500,-63315000,0),(-97526400,-63314800,0)]
  Start = (-9.7527e+07,-6.33151e+07,0)
  Subdivisions = 0
FEATURE [Part::Part2DObjectPython] DWire035  label="25.079"  # Draft 2D object (typed FeaturePython)
  ChamferSize = 0
  Closed = true
  End = (-9.75157e+07,-6.33084e+07,0)
  FilletRadius = 0
  Length = 5381.21
  MakeFace = false
  Points = (4) [(-97517100,-63309100,0),(-97516200,-63310000,0),(-97515500,-63310200,0),(-97515700,-63308400,0)]
  Start = (-9.75171e+07,-6.33091e+07,0)
  Subdivisions = 0
FEATURE [Part::Part2DObjectPython] DWire036  label="25.080"  # Draft 2D object (typed FeaturePython)
  ChamferSize = 0
  Closed = true
  End = (-97510608,-63305988,25750)
  FilletRadius = 0
  Length = 174553
  MakeFace = false
  Points = (71) [(-97509100,-63305100,25750),(-97508000,-63307600,25750),(-97507700,-63308000,25750),(-97510500,-63308200,25750),(-97511200,-63312200,25750),+66 more]
  Start = (-9.75091e+07,-6.33051e+07,25750)
  Subdivisions = 0
FEATURE [Part::Part2DObjectPython] DWire037  label="LIMITE"  # Draft 2D object (typed FeaturePython)
  ChamferSize = 0
  Closed = true
  End = (-9.75482e+07,-6.33327e+07,25000)
  FilletRadius = 0
  Length = 431357
  MakeFace = false
  Points = (49) [(-97554800,-63336300,25000),(-97558200,-63329200,25000),(-97550300,-63325600,25000),(-97539000,-63320500,25000),(-97523800,-63313700,25000),+44 more]
  Start = (-9.75548e+07,-6.33363e+07,25000)
  Subdivisions = 0
FEATURE [Part::Part2DObjectPython] DWire039  label="27.5"  # Draft 2D object (typed FeaturePython)
  ChamferSize = 0
  Closed = true
  End = (-9.74628e+07,-6.33654e+07,27500)
  FilletRadius = 0
  Length = 33256.2
  MakeFace = false
  Points = (9) [(-97468200,-63366300,27500),(-97468200,-63363500,27500),(-97468100,-63363200,27500),(-97467300,-63361300,27500),(-97466900,-63361300,27500),+4 more]
  Start = (-9.74682e+07,-6.33663e+07,27500)
  Subdivisions = 0
FEATURE [Part::Part2DObjectPython] DWire040  label="27.25"  # Draft 2D object (typed FeaturePython)
  ChamferSize = 0
  Closed = true
  End = (-97468304,-63368080,27250)
  FilletRadius = 0
  Length = 59349.9
  MakeFace = false
  Points = (15) [(-97475200,-63369300,27250),(-97475200,-63367900,27250),(-97474900,-63366400,27250),(-97474000,-63364200,27250),(-97469800,-63354300,27250),+10 more]
  Start = (-9.74752e+07,-6.33693e+07,27250)
  Subdivisions = 0
FEATURE [Part::Part2DObjectPython] DWire041  label="27"  # Draft 2D object (typed FeaturePython)
  ChamferSize = 0
  Closed = true
  End = (-9.74826e+07,-6.34004e+07,27000)
  FilletRadius = 0
  Length = 151957
  MakeFace = false
  Points = (26) [(-97482600,-63399200,27000),(-97482300,-63380200,27000),(-97482300,-63376800,27000),(-97482000,-63370800,27000),(-97481700,-63369600,27000),+21 more]
  Start = (-9.74826e+07,-6.33992e+07,27000)
  Subdivisions = 0
FEATURE [Part::Part2DObjectPython] DWire042  label="26.75"  # Draft 2D object (typed FeaturePython)
  ChamferSize = 0
  Closed = true
  End = (-9.74708e+07,-6.33418e+07,26750)
  FilletRadius = 0
  Length = 233656
  MakeFace = false
  Points = (56) [(-97472500,-63335400,26750),(-97473100,-63335700,26750),(-97474700,-63335800,26750),(-97473900,-63337300,26750),(-97474700,-63338400,26750),+51 more]
  Start = (-97472512,-63335368,26750)
  Subdivisions = 0
FEATURE [Part::Part2DObjectPython] DWire043  label="26.5"  # Draft 2D object (typed FeaturePython)
  ChamferSize = 0
  Closed = true
  End = (-97473952,-6.333e+07,26500)
  FilletRadius = 0
  Length = 258906
  MakeFace = false
  Points = (66) [(-97476800,-63319400,26500),(-97477700,-63319700,26500),(-97477800,-63320000,26500),(-97477700,-63321800,26500),(-97477500,-63321700,26500),+61 more]
  Start = (-97476752,-63319380,26500)
  Subdivisions = 0
FEATURE [Part::Part2DObjectPython] DWire044  label="26.25"  # Draft 2D object (typed FeaturePython)
  ChamferSize = 0
  Closed = true
  End = (-9.75074e+07,-6.33998e+07,26250)
  FilletRadius = 0
  Length = 342559
  MakeFace = false
  Points = (64) [(-97522900,-63398500,26250),(-97520200,-63395300,26250),(-97515100,-63393100,26250),(-97515800,-63389100,26250),(-97512800,-63380600,26250),+59 more]
  Start = (-97522904,-63398528,26250)
  Subdivisions = 0
FEATURE [Part::Part2DObjectPython] DWire045  label="26.076"  # Draft 2D object (typed FeaturePython)
  ChamferSize = 0
  Closed = true
  End = (-9.75443e+07,-6.3378e+07,26250)
  FilletRadius = 0
  Length = 3404.63
  MakeFace = false
  Points = (3) [(-97544700,-63378000,26250),(-97544500,-63379500,26250),(-97544300,-63378000,26250)]
  Start = (-9.75447e+07,-6.3378e+07,26250)
  Subdivisions = 0
FEATURE [Part::Part2DObjectPython] DWire046  label="26.077"  # Draft 2D object (typed FeaturePython)
  ChamferSize = 0
  Closed = true
  End = (-9.75346e+07,-6.33254e+07,26250)
  FilletRadius = 0
  Length = 709.541
  MakeFace = false
  Points = (3) [(-97534300,-63325200,26250),(-97534400,-63325200,26250),(-97534600,-63325400,26250)]
  Start = (-9.75343e+07,-6.33252e+07,26250)
  Subdivisions = 0
FEATURE [Part::Part2DObjectPython] DWire047  label="26"  # Draft 2D object (typed FeaturePython)
  ChamferSize = 0
  Closed = true
  End = (-9.75074e+07,-6.33998e+07,26000)
  FilletRadius = 0
  Length = 365101
  MakeFace = false
  Points = (94) [(-97539500,-63397100,26000),(-97539200,-63397000,26000),(-97530400,-63393100,26000),(-97530700,-63391700,26000),(-97527100,-63381500,26000),+89 more]
  Start = (-97539488,-63397136,26000)
  Subdivisions = 0
FEATURE [Part::Part2DObjectPython] DWire049  label="26001"  # Draft 2D object (typed FeaturePython)
  ChamferSize = 0
  Closed = true
  End = (-9.75475e+07,-6.33782e+07,26000)
  FilletRadius = 0
  Length = 26505.2
  MakeFace = false
  Points = (8) [(-97546000,-63388700,26000),(-97544100,-63378200,26000),(-97543400,-63378000,26000),(-97543400,-63377800,26000),(-97543700,-63377900,26000),+3 more]
  Start = (-9.7546e+07,-6.33887e+07,26000)
  Subdivisions = 0
FEATURE [Part::Part2DObjectPython] DWire050  label="26002"  # Draft 2D object (typed FeaturePython)
  ChamferSize = 0
  Closed = true
  End = (-97532096,-63325532,26000)
  FilletRadius = 0
  Length = 921.494
  MakeFace = false
  Points = (4) [(-97532100,-63325500,26000),(-97532400,-63325400,26000),(-97532200,-63325800,26000),(-97532100,-63325500,26000)]
  Start = (-9.75321e+07,-6.33255e+07,26000)
  Subdivisions = 0
FEATURE [Part::Part2DObjectPython] DWire051  label="26003"  # Draft 2D object (typed FeaturePython)
  ChamferSize = 0
  Closed = true
  End = (-9.75378e+07,-6.33271e+07,26000)
  FilletRadius = 0
  Length = 10949.8
  MakeFace = false
  Points = (4) [(-97533600,-63324900,26000),(-97535500,-63324200,26000),(-97538100,-63327100,26000),(-97537800,-63327100,26000)]
  Start = (-9.75336e+07,-6.33249e+07,26000)
  Subdivisions = 0
FEATURE [Part::Part2DObjectPython] DWire052  label="26004"  # Draft 2D object (typed FeaturePython)
  ChamferSize = 0
  Closed = true
  End = (-9.75516e+07,-6.33346e+07,26000)
  FilletRadius = 0
  Length = 74680
  MakeFace = false
  Points = (18) [(-97541000,-63328900,26000),(-97545800,-63329200,26000),(-97548900,-63328700,26000),(-97550700,-63328900,26000),(-97551100,-63326400,26000),+13 more]
  Start = (-9.7541e+07,-6.33289e+07,26000)
  Subdivisions = 0
FEATURE [Part::Part2DObjectPython] DWire053  label="26005"  # Draft 2D object (typed FeaturePython)
  ChamferSize = 0
  Closed = true
  End = (-9.75357e+07,-6.33465e+07,26000)
  FilletRadius = 0
  Length = 79800.8
  MakeFace = false
  Points = (15) [(-97541900,-63374300,26000),(-97540600,-63371900,26000),(-97538400,-63369600,26000),(-97540400,-63367900,26000),(-97539500,-63364400,26000),+10 more]
  Start = (-9.75419e+07,-6.33743e+07,26000)
  Subdivisions = 0
FEATURE [App::DocumentObjectGroup] Group004  label="curvas_nivel"
  Group = -> [DWire030,DWire031,DWire032,DWire033,DWire034,DWire035,DWire036,DWire039,DWire043,DWire040,DWire041,DWire042,DWire052,DWire053,DWire050,DWire049,DWire051,DWire046,DWire045,DWire047,DWire044,DWire037]
FEATURE [App::FeaturePython] Dimension  # Draft dimension (typed FeaturePython)
  Dimline = (-97527464,-63336800,26000)
  Direction = (0,0,0)
  Distance = 1671.84
  End = (-9.75266e+07,-6.33366e+07,26000)
  Normal = (0,0,1)
  Start = (-9.75282e+07,-6.33363e+07,26000)
FEATURE [Part::Part2DObjectPython] Line004  # Draft 2D object (typed FeaturePython)
  ChamferSize = 0
  Closed = false
  End = (-9.75363e+07,-6.33734e+07,26000)
  FilletRadius = 0
  Length = 3835.25
  MakeFace = true
  Points = (2) [(-97535500,-63369700,26000),(-97536300,-63373400,26000)]
  Start = (-9.75355e+07,-6.33697e+07,26000)
  Subdivisions = 0
FEATURE [Part::Part2DObjectPython] Line005  # Draft 2D object (typed FeaturePython)
  ChamferSize = 0
  Closed = false
  End = (-9.75343e+07,-6.33738e+07,26000)
  FilletRadius = 0
  Length = 3835.25
  MakeFace = true
  Points = (2) [(-97533500,-63370100,26000),(-97534300,-63373800,26000)]
  Start = (-9.75335e+07,-6.33701e+07,26000)
  Subdivisions = 0
FEATURE [Part::Part2DObjectPython] Rectangle001  # Draft 2D object (typed FeaturePython)
  ChamferSize = 0
  Columns = 1
  FilletRadius = 0
  Height = 8000
  Length = 40000
  MakeFace = true
  Placement = pos=(-9.75257e+07,-6.33718e+07,26000) rot=(0,0,1;1.35374rad)
  Rows = 1
FEATURE [Part::Extrusion] Extrude021
  Base = -> Rectangle001
  Dir = (0,0,10000)
  Solid = true
FEATURE [Part::Part2DObjectPython] DWire054  # Draft 2D object (typed FeaturePython)
  ChamferSize = 0
  Closed = true
  End = (-9.75201e+07,-6.33464e+07,26000)
  FilletRadius = 0
  Length = 112683
  MakeFace = true
  Points = (8) [(-97525700,-63371800,26000),(-97495200,-63371800,26000),(-97489800,-63371400,26000),(-97489600,-63366600,26000),(-97491000,-63366600,26000),+3 more]
  Start = (-9.75257e+07,-6.33718e+07,26000)
  Subdivisions = 0
FEATURE [Part::Extrusion] Extrude022
  Base = -> DWire054
  Dir = (0,0,7000)
  Solid = true
FEATURE [Part::Part2DObjectPython] Rectangle002  # Draft 2D object (typed FeaturePython)
  ChamferSize = 0
  Columns = 1
  FilletRadius = 0
  Height = 12237.7
  Length = 25081.9
  MakeFace = true
  Placement = pos=(-97491256,-63324944,26000) rot=(0,0,-1;1.32599rad)
  Rows = 1
FEATURE [Part::Extrusion] Extrude023
  Base = -> Rectangle002
  Dir = (0,0,9000)
  Solid = true
FEATURE [Part::Part2DObjectPython] Rectangle  # Draft 2D object (typed FeaturePython)
  ChamferSize = 0
  Columns = 1
  FilletRadius = 0
  Height = 7000
  Length = -40000
  MakeFace = true
  Placement = pos=(-97473304,-63346312,26000) rot=(0,0,1;0.259343rad)
  Rows = 1
FEATURE [Part::Extrusion] Extrude024
  Base = -> Rectangle
  Dir = (0,0,12000)
  Solid = true
FEATURE [Part::Part2DObjectPython] Rectangle005  # Draft 2D object (typed FeaturePython)
  ChamferSize = 0
  Columns = 1
  FilletRadius = 0
  Height = 4000
  Length = -16000
  MakeFace = true
  Placement = pos=(-9.75057e+07,-6.33313e+07,26000) rot=(0,0,1;3.3438rad)
  Rows = 1
FEATURE [Part::Part2DObjectPython] Rectangle006  # Draft 2D object (typed FeaturePython)
  ChamferSize = 0
  Columns = 1
  FilletRadius = 0
  Height = 4000
  Length = 20000
  MakeFace = true
  Placement = pos=(-9.75017e+07,-6.33305e+07,26000) rot=(0,0,1;1.80398rad)
  Rows = 1
FEATURE [Part::Extrusion] Extrude025
  Base = -> Rectangle006
  Dir = (0,0,5000)
  Solid = true
FEATURE [Part::Extrusion] Extrude026
  Base = -> Rectangle005
  Dir = (0,0,5000)
  Solid = true
FEATURE [Part::Part2DObjectPython] DWire056  # Draft 2D object (typed FeaturePython)
  ChamferSize = 0
  Closed = true
  End = (-9.74968e+07,-6.3323e+07,26000)
  FilletRadius = 0
  Length = 45292.2
  MakeFace = true
  Points = (5) [(-97503200,-63324200,26000),(-97506400,-63311000,26000),(-97506600,-63310200,26000),(-97499600,-63306700,26000),(-97496800,-63323000,26000)]
  Start = (-97503250,-63324150,26000)
  Subdivisions = 0
FEATURE [Part::Extrusion] Extrude027
  Base = -> DWire056
  Dir = (0,0,7000)
  Solid = true
FEATURE [Part::Part2DObjectPython] DWire057  # Draft 2D object (typed FeaturePython)
  ChamferSize = 0
  Closed = true
  End = (-9.75009e+07,-6.33784e+07,26000)
  FilletRadius = 0
  Length = 123852
  MakeFace = true
  Points = (8) [(-97501100,-63373600,26000),(-97518800,-63326900,26000),(-97515100,-63325400,26000),(-97494800,-63352000,26000),(-97495900,-63365700,26000),+3 more]
  Start = (-9.75011e+07,-6.33736e+07,26000)
  Subdivisions = 0
FEATURE [Part::Extrusion] Extrude028
  Base = -> DWire057
  Dir = (0,0,4000)
  Solid = true
FEATURE [Part::Cut] Cut
  Base = -> Extrude022
  Tool = -> Extrude028
FEATURE [Part::FeaturePython] Clone001  label="Clone of Extrude028"  # Draft clone (typed FeaturePython)
  Objects = -> [Extrude028]
  Scale = (1,1,1)
FEATURE [Part::Cut] Cut001
  Base = -> Extrude024
  Tool = -> Clone001
FEATURE [App::DocumentObjectGroup] Group005  label="volumes_proposta"
  Group = -> [Extrude021,Extrude023,Extrude025,Extrude026,Extrude027,Cut,Cut001]
FEATURE [Part::Part2DObjectPython] DWire058  # Draft 2D object (typed FeaturePython)
  ChamferSize = 0
  Closed = true
  End = (-97511904,-63375524,37810)
  FilletRadius = 0
  Length = 84508.6
  MakeFace = false
  Points = (4) [(-97537600,-63377700,37810),(-97538300,-63393200,37810),(-97511300,-63391700,37810),(-97511900,-63375500,37810)]
  Start = (-9.75376e+07,-6.33777e+07,37810)
  Subdivisions = 0
FEATURE [Part::FeaturePython] Roof  # WARN: FeaturePython — macro-defined, semantics opaque (R4)
  Angles = [90,30,90,30]
  Base = -> DWire058
  Face = 0
  Heights = [0,4907.48,0,4907.48]
  IdRel = [0,0,0,0]
  MoveWithHost = false
  Overhang = [-700,250,100,250]
  Role = 0
  Runs = [8500,8500,8500,8500]
  Thickness = [100,100,100,100]
FEATURE [Part::FeaturePython] Wall  # WARN: FeaturePython — macro-defined, semantics opaque (R4)
  Align = 2
  Base = -> Extrude009
  Face = 0
  Height = 3000
  Length = 0
  MoveWithHost = false
  Normal = (0,0,0)
  Role = 0
  Subtractions = -> [Roof]
  Width = 200
FEATURE [Part::Part2DObjectPython] DWire059  # Draft 2D object (typed FeaturePython)
  ChamferSize = 0
  Closed = true
  End = (-97538296,-63393164,37810)
  FilletRadius = 0
  Length = 19928.2
  MakeFace = false
  Points = (4) [(-97538100,-63388000,37810),(-97533300,-63388000,37810),(-97533300,-63392900,37810),(-97538300,-63393200,37810)]
  Start = (-9.75381e+07,-6.3388e+07,37810)
  Subdivisions = 0
FEATURE [Part::Extrusion] Extrusion007
  Base = -> DWire059
  Dir = (0,0,9000)
  Solid = true
FEATURE [Part::MultiFuse] Fusion
  Shapes = -> [Extrusion007,Wall]
FEATURE [App::DocumentObjectGroupPython] Building  # scripted group (container) (typed FeaturePython)
  BuildingType = 80
  Group = -> [Fusion]
  Height = 0
FEATURE [App::DocumentObjectGroup] Group003  label="volumes"
  Group = -> [Extrusion006,Extrude007,Extrude,Extrude001,DWire001,Extrude002,Line,DWire002,Extrude003,DWire003,Extrude004,Extrude005,Extrude006,Extrude008,DWire009,Extrude009,Line001,Line003,Compound,Extrude010,Extrusion005,Extrusion004,Extrusion003,Extrude020,Extrusion001,Extrusion,DWire019,Extrude018,DWire020,Extrude017,Extrude016,Extrude015,DWire014,Extrude012,Extrude013,DWire021,Extrude014,Extrude011,Roof,+2 more]
FEATURE [App::FeaturePython] Section  label="Section1"  # WARN: FeaturePython — macro-defined, semantics opaque (R4)
  Objects = -> [Extrude028,Group005,Group003]
  OnlySolids = true
  Placement = pos=(-9.75097e+07,-6.33499e+07,28000) rot=(0.71527,-0.49416,-0.49416;1.89979rad)
FEATURE [App::FeaturePython] Section001  label="Section2"  # WARN: FeaturePython — macro-defined, semantics opaque (R4)
  Objects = -> [Cut,Group005,Group003]
  OnlySolids = true
  Placement = pos=(-9.75059e+07,-6.33598e+07,28000) rot=(0.438943,0.635346,0.635346;2.31435rad)
FEATURE [App::FeaturePython] Section002  label="Section"  # WARN: FeaturePython — macro-defined, semantics opaque (R4)
  Objects = -> [Cut001]
  OnlySolids = true
  Placement = pos=(-97491500,-63200000,32512.4) rot=(0.983417,0.128241,0.128241;1.58752rad)
